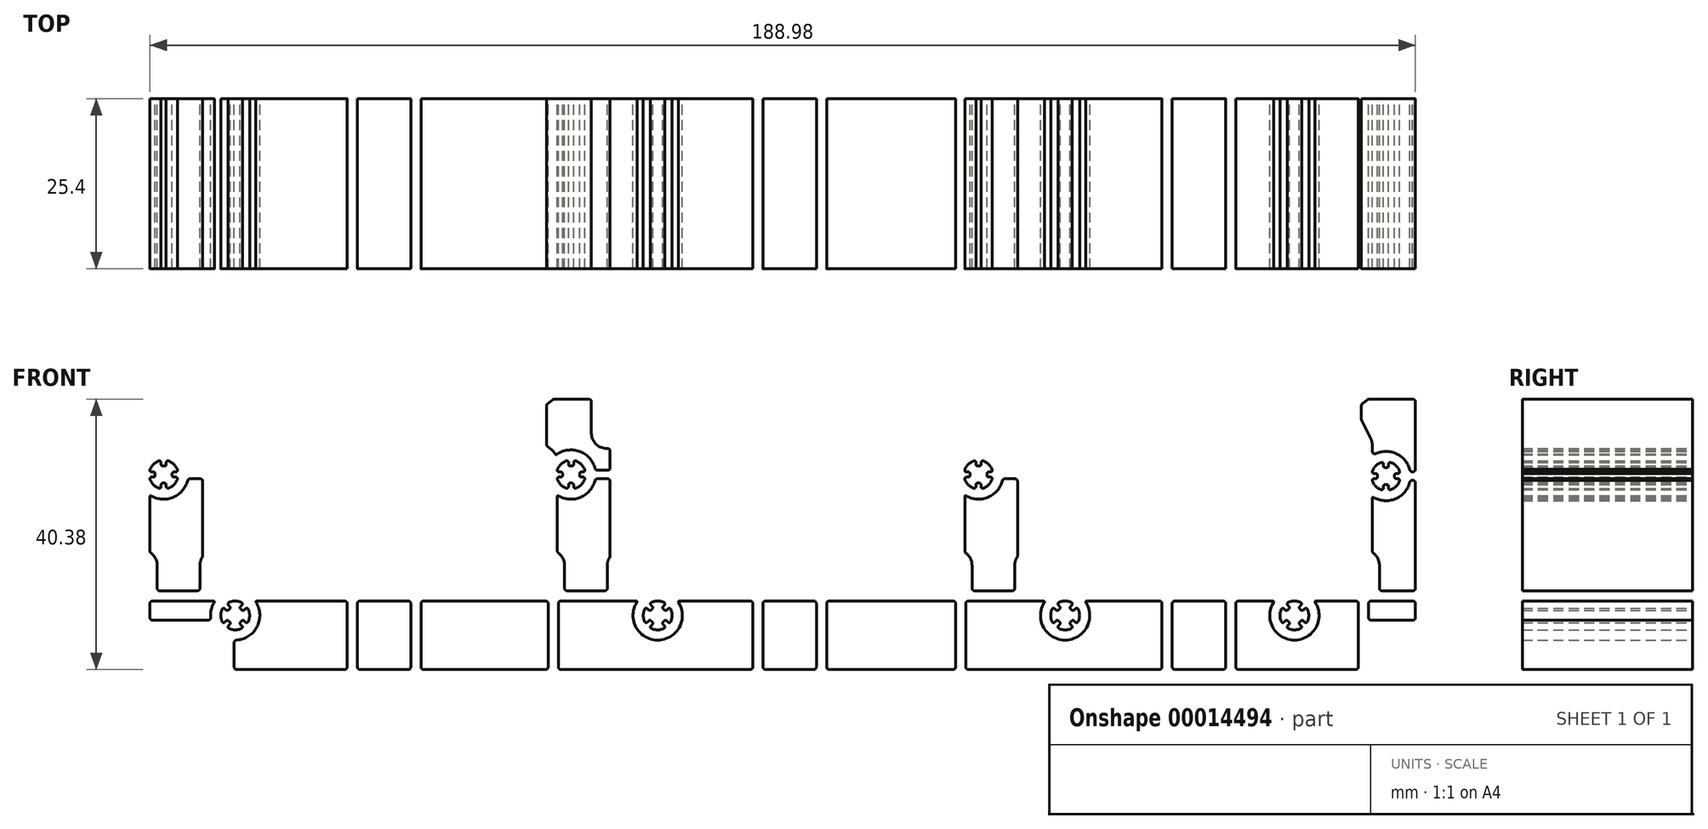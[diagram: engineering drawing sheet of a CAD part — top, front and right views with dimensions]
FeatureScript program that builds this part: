
annotation { "Feature Type Name" : "Feature", "Feature Type Description" : "" }
export const myFeature = defineFeature(function(context is Context, id is Id, definition is map)
    precondition{}
    {
        {
            var Q0;
            Q0=qCreatedBy(makeId("Front.planeOp"),FACE);
            var sketch = newSketch(context, id + "F0", { "sketchPlane" : qUnion([Q0])});
            skArc(sketch, "E0", {"start": v(5.84, 2.36) * mm, "mid": v(5.73, 2.63) * mm, "end": v(5.46, 2.75) * mm});
            skLineSegment(sketch, "E1", {"start": v(5.46, 2.75) * mm, "end": v(-1.75, 2.75) * mm});
            skArc(sketch, "E2", {"start": v(-1.75, 2.75) * mm, "mid": v(-2.02, 2.63) * mm, "end": v(-2.13, 2.36) * mm});
            skLineSegment(sketch, "E3", {"start": v(-2.13, 2.36) * mm, "end": v(-2.13, -7.1) * mm});
            skArc(sketch, "E4", {"start": v(-2.13, -7.1) * mm, "mid": v(-2.02, -7.38) * mm, "end": v(-1.75, -7.5) * mm});
            skLineSegment(sketch, "E5", {"start": v(-1.75, -7.5) * mm, "end": v(5.46, -7.5) * mm});
            skArc(sketch, "E6", {"start": v(5.46, -7.5) * mm, "mid": v(5.73, -7.38) * mm, "end": v(5.84, -7.1) * mm});
            skLineSegment(sketch, "E7", {"start": v(5.84, -7.1) * mm, "end": v(5.84, 2.36) * mm});
            skArc(sketch, "E8", {"start": v(-3.66, 2.36) * mm, "mid": v(-3.77, 2.63) * mm, "end": v(-4.04, 2.75) * mm});
            skLineSegment(sketch, "E9", {"start": v(-4.04, 2.75) * mm, "end": v(-14.63, 2.75) * mm});
            skArc(sketch, "E10", {"start": v(-14.63, 2.75) * mm, "mid": v(-14.74, 2.68) * mm, "end": v(-14.74, 2.55) * mm});
            skArc(sketch, "E11", {"start": v(-20.97, 2.55) * mm, "mid": v(-17.85, -3.1) * mm, "end": v(-14.74, 2.55) * mm});
            skArc(sketch, "E12", {"start": v(-20.97, 2.55) * mm, "mid": v(-20.96, 2.68) * mm, "end": v(-21.07, 2.75) * mm});
            skLineSegment(sketch, "E13", {"start": v(-21.07, 2.75) * mm, "end": v(-32.3, 2.75) * mm});
            skArc(sketch, "E14", {"start": v(-32.3, 2.75) * mm, "mid": v(-32.58, 2.63) * mm, "end": v(-32.69, 2.36) * mm});
            skLineSegment(sketch, "E15", {"start": v(-32.69, 2.36) * mm, "end": v(-32.69, -7.1) * mm});
            skArc(sketch, "E16", {"start": v(-32.69, -7.1) * mm, "mid": v(-32.58, -7.38) * mm, "end": v(-32.3, -7.5) * mm});
            skLineSegment(sketch, "E17", {"start": v(-32.3, -7.5) * mm, "end": v(-4.04, -7.5) * mm});
            skArc(sketch, "E18", {"start": v(-4.04, -7.5) * mm, "mid": v(-3.77, -7.38) * mm, "end": v(-3.66, -7.1) * mm});
            skLineSegment(sketch, "E19", {"start": v(-3.66, -7.1) * mm, "end": v(-3.66, 2.36) * mm});
            skArc(sketch, "E20", {"start": v(-15.9, 1.51) * mm, "mid": v(-16.1, 1.66) * mm, "end": v(-16.31, 1.58) * mm});
            skLineSegment(sketch, "E21", {"start": v(-16.31, 1.58) * mm, "end": v(-16.5, 1.4) * mm});
            skArc(sketch, "E22", {"start": v(-16.87, 1.4) * mm, "mid": v(-16.69, 1.32) * mm, "end": v(-16.5, 1.4) * mm});
            skLineSegment(sketch, "E23", {"start": v(-16.87, 1.4) * mm, "end": v(-17.04, 1.57) * mm});
            skArc(sketch, "E24", {"start": v(-17.04, 1.93) * mm, "mid": v(-17.12, 1.75) * mm, "end": v(-17.04, 1.57) * mm});
            skLineSegment(sketch, "E25", {"start": v(-17.04, 1.93) * mm, "end": v(-16.85, 2.12) * mm});
            skArc(sketch, "E26", {"start": v(-16.85, 2.12) * mm, "mid": v(-16.78, 2.35) * mm, "end": v(-16.92, 2.53) * mm});
            skArc(sketch, "E27", {"start": v(-16.92, 2.53) * mm, "mid": v(-17.85, 2.74) * mm, "end": v(-18.78, 2.53) * mm});
            skArc(sketch, "E28", {"start": v(-18.78, 2.53) * mm, "mid": v(-18.92, 2.35) * mm, "end": v(-18.85, 2.12) * mm});
            skLineSegment(sketch, "E29", {"start": v(-18.85, 2.12) * mm, "end": v(-18.66, 1.93) * mm});
            skArc(sketch, "E30", {"start": v(-18.66, 1.57) * mm, "mid": v(-18.59, 1.75) * mm, "end": v(-18.66, 1.93) * mm});
            skLineSegment(sketch, "E31", {"start": v(-18.66, 1.57) * mm, "end": v(-18.84, 1.4) * mm});
            skArc(sketch, "E32", {"start": v(-19.2, 1.4) * mm, "mid": v(-19.02, 1.32) * mm, "end": v(-18.84, 1.4) * mm});
            skLineSegment(sketch, "E33", {"start": v(-19.2, 1.4) * mm, "end": v(-19.4, 1.58) * mm});
            skArc(sketch, "E34", {"start": v(-19.4, 1.58) * mm, "mid": v(-19.62, 1.66) * mm, "end": v(-19.8, 1.51) * mm});
            skArc(sketch, "E35", {"start": v(-19.8, 1.51) * mm, "mid": v(-20.01, 0.58) * mm, "end": v(-19.8, -0.35) * mm});
            skArc(sketch, "E36", {"start": v(-19.8, -0.35) * mm, "mid": v(-19.62, -0.49) * mm, "end": v(-19.4, -0.42) * mm});
            skLineSegment(sketch, "E37", {"start": v(-19.4, -0.42) * mm, "end": v(-19.2, -0.22) * mm});
            skArc(sketch, "E38", {"start": v(-18.84, -0.22) * mm, "mid": v(-19.02, -0.15) * mm, "end": v(-19.2, -0.22) * mm});
            skLineSegment(sketch, "E39", {"start": v(-18.84, -0.22) * mm, "end": v(-18.66, -0.4) * mm});
            skArc(sketch, "E40", {"start": v(-18.66, -0.76) * mm, "mid": v(-18.59, -0.58) * mm, "end": v(-18.66, -0.4) * mm});
            skLineSegment(sketch, "E41", {"start": v(-18.66, -0.76) * mm, "end": v(-18.85, -0.96) * mm});
            skArc(sketch, "E42", {"start": v(-18.85, -0.96) * mm, "mid": v(-18.92, -1.18) * mm, "end": v(-18.78, -1.36) * mm});
            skArc(sketch, "E43", {"start": v(-18.78, -1.36) * mm, "mid": v(-17.85, -1.57) * mm, "end": v(-16.92, -1.36) * mm});
            skArc(sketch, "E44", {"start": v(-16.92, -1.36) * mm, "mid": v(-16.78, -1.18) * mm, "end": v(-16.85, -0.96) * mm});
            skLineSegment(sketch, "E45", {"start": v(-16.85, -0.96) * mm, "end": v(-17.04, -0.76) * mm});
            skArc(sketch, "E46", {"start": v(-17.04, -0.4) * mm, "mid": v(-17.12, -0.58) * mm, "end": v(-17.04, -0.76) * mm});
            skLineSegment(sketch, "E47", {"start": v(-17.04, -0.4) * mm, "end": v(-16.87, -0.22) * mm});
            skArc(sketch, "E48", {"start": v(-16.5, -0.22) * mm, "mid": v(-16.69, -0.15) * mm, "end": v(-16.87, -0.22) * mm});
            skLineSegment(sketch, "E49", {"start": v(-16.5, -0.22) * mm, "end": v(-16.31, -0.42) * mm});
            skArc(sketch, "E50", {"start": v(-16.31, -0.42) * mm, "mid": v(-16.1, -0.49) * mm, "end": v(-15.9, -0.35) * mm});
            skArc(sketch, "E51", {"start": v(-15.9, -0.35) * mm, "mid": v(-15.7, 0.58) * mm, "end": v(-15.9, 1.51) * mm});
            skArc(sketch, "E52", {"start": v(-34.21, 2.36) * mm, "mid": v(-34.32, 2.63) * mm, "end": v(-34.6, 2.75) * mm});
            skLineSegment(sketch, "E53", {"start": v(-34.6, 2.75) * mm, "end": v(-52.82, 2.75) * mm});
            skArc(sketch, "E54", {"start": v(-52.82, 2.75) * mm, "mid": v(-53.09, 2.63) * mm, "end": v(-53.2, 2.36) * mm});
            skLineSegment(sketch, "E55", {"start": v(-53.2, 2.36) * mm, "end": v(-53.2, -7.1) * mm});
            skArc(sketch, "E56", {"start": v(-53.2, -7.1) * mm, "mid": v(-53.09, -7.38) * mm, "end": v(-52.82, -7.5) * mm});
            skLineSegment(sketch, "E57", {"start": v(-52.82, -7.5) * mm, "end": v(-34.6, -7.5) * mm});
            skArc(sketch, "E58", {"start": v(-34.6, -7.5) * mm, "mid": v(-34.32, -7.38) * mm, "end": v(-34.21, -7.1) * mm});
            skLineSegment(sketch, "E59", {"start": v(-34.21, -7.1) * mm, "end": v(-34.21, 2.36) * mm});
            skArc(sketch, "E60", {"start": v(-54.72, 2.36) * mm, "mid": v(-54.84, 2.63) * mm, "end": v(-55.1, 2.75) * mm});
            skLineSegment(sketch, "E61", {"start": v(-55.1, 2.75) * mm, "end": v(-62.32, 2.75) * mm});
            skArc(sketch, "E62", {"start": v(-62.32, 2.75) * mm, "mid": v(-62.59, 2.63) * mm, "end": v(-62.7, 2.36) * mm});
            skLineSegment(sketch, "E63", {"start": v(-62.7, 2.36) * mm, "end": v(-62.7, -7.1) * mm});
            skArc(sketch, "E64", {"start": v(-62.7, -7.1) * mm, "mid": v(-62.59, -7.38) * mm, "end": v(-62.32, -7.5) * mm});
            skLineSegment(sketch, "E65", {"start": v(-62.32, -7.5) * mm, "end": v(-55.1, -7.5) * mm});
            skArc(sketch, "E66", {"start": v(-55.1, -7.5) * mm, "mid": v(-54.84, -7.38) * mm, "end": v(-54.72, -7.1) * mm});
            skLineSegment(sketch, "E67", {"start": v(-54.72, -7.1) * mm, "end": v(-54.72, 2.36) * mm});
            skArc(sketch, "E68", {"start": v(-64.22, 2.36) * mm, "mid": v(-64.33, 2.63) * mm, "end": v(-64.6, 2.75) * mm});
            skLineSegment(sketch, "E69", {"start": v(-64.6, 2.75) * mm, "end": v(-77.73, 2.75) * mm});
            skArc(sketch, "E70", {"start": v(-77.73, 2.75) * mm, "mid": v(-77.84, 2.68) * mm, "end": v(-77.84, 2.55) * mm});
            skArc(sketch, "E71", {"start": v(-80.74, -3.1) * mm, "mid": v(-77.68, -1.1) * mm, "end": v(-77.84, 2.55) * mm});
            skArc(sketch, "E72", {"start": v(-80.74, -3.1) * mm, "mid": v(-81, -3.2) * mm, "end": v(-81.1, -3.47) * mm});
            skLineSegment(sketch, "E73", {"start": v(-81.1, -3.47) * mm, "end": v(-81.1, -7.1) * mm});
            skArc(sketch, "E74", {"start": v(-81.1, -7.1) * mm, "mid": v(-81, -7.38) * mm, "end": v(-80.72, -7.5) * mm});
            skLineSegment(sketch, "E75", {"start": v(-80.72, -7.5) * mm, "end": v(-64.6, -7.5) * mm});
            skArc(sketch, "E76", {"start": v(-64.6, -7.5) * mm, "mid": v(-64.33, -7.38) * mm, "end": v(-64.22, -7.1) * mm});
            skLineSegment(sketch, "E77", {"start": v(-64.22, -7.1) * mm, "end": v(-64.22, 2.36) * mm});
            skArc(sketch, "E78", {"start": v(-79, 1.52) * mm, "mid": v(-79.19, 1.66) * mm, "end": v(-79.41, 1.59) * mm});
            skLineSegment(sketch, "E79", {"start": v(-79.41, 1.59) * mm, "end": v(-79.6, 1.4) * mm});
            skArc(sketch, "E80", {"start": v(-79.96, 1.4) * mm, "mid": v(-79.78, 1.32) * mm, "end": v(-79.6, 1.4) * mm});
            skLineSegment(sketch, "E81", {"start": v(-79.96, 1.4) * mm, "end": v(-80.14, 1.57) * mm});
            skArc(sketch, "E82", {"start": v(-80.14, 1.93) * mm, "mid": v(-80.22, 1.75) * mm, "end": v(-80.14, 1.57) * mm});
            skLineSegment(sketch, "E83", {"start": v(-80.14, 1.93) * mm, "end": v(-79.95, 2.13) * mm});
            skArc(sketch, "E84", {"start": v(-79.95, 2.13) * mm, "mid": v(-79.88, 2.35) * mm, "end": v(-80.02, 2.53) * mm});
            skArc(sketch, "E85", {"start": v(-80.02, 2.53) * mm, "mid": v(-80.95, 2.75) * mm, "end": v(-81.88, 2.53) * mm});
            skArc(sketch, "E86", {"start": v(-81.88, 2.53) * mm, "mid": v(-82.02, 2.35) * mm, "end": v(-81.95, 2.13) * mm});
            skLineSegment(sketch, "E87", {"start": v(-81.95, 2.13) * mm, "end": v(-81.76, 1.93) * mm});
            skArc(sketch, "E88", {"start": v(-81.76, 1.57) * mm, "mid": v(-81.69, 1.75) * mm, "end": v(-81.76, 1.93) * mm});
            skLineSegment(sketch, "E89", {"start": v(-81.76, 1.57) * mm, "end": v(-81.94, 1.4) * mm});
            skArc(sketch, "E90", {"start": v(-82.3, 1.4) * mm, "mid": v(-82.12, 1.32) * mm, "end": v(-81.94, 1.4) * mm});
            skLineSegment(sketch, "E91", {"start": v(-82.3, 1.4) * mm, "end": v(-82.5, 1.59) * mm});
            skArc(sketch, "E92", {"start": v(-82.5, 1.59) * mm, "mid": v(-82.71, 1.66) * mm, "end": v(-82.9, 1.52) * mm});
            skArc(sketch, "E93", {"start": v(-82.9, 1.52) * mm, "mid": v(-83.11, 0.59) * mm, "end": v(-82.9, -0.34) * mm});
            skArc(sketch, "E94", {"start": v(-82.9, -0.34) * mm, "mid": v(-82.71, -0.49) * mm, "end": v(-82.5, -0.41) * mm});
            skLineSegment(sketch, "E95", {"start": v(-82.5, -0.41) * mm, "end": v(-82.3, -0.22) * mm});
            skArc(sketch, "E96", {"start": v(-81.94, -0.22) * mm, "mid": v(-82.12, -0.15) * mm, "end": v(-82.3, -0.22) * mm});
            skLineSegment(sketch, "E97", {"start": v(-81.94, -0.22) * mm, "end": v(-81.76, -0.4) * mm});
            skArc(sketch, "E98", {"start": v(-81.76, -0.76) * mm, "mid": v(-81.69, -0.58) * mm, "end": v(-81.76, -0.4) * mm});
            skLineSegment(sketch, "E99", {"start": v(-81.76, -0.76) * mm, "end": v(-81.95, -0.95) * mm});
            skArc(sketch, "E100", {"start": v(-81.95, -0.95) * mm, "mid": v(-82.02, -1.18) * mm, "end": v(-81.88, -1.36) * mm});
            skArc(sketch, "E101", {"start": v(-81.88, -1.36) * mm, "mid": v(-80.95, -1.57) * mm, "end": v(-80.02, -1.36) * mm});
            skArc(sketch, "E102", {"start": v(-80.02, -1.36) * mm, "mid": v(-79.88, -1.18) * mm, "end": v(-79.95, -0.95) * mm});
            skLineSegment(sketch, "E103", {"start": v(-79.95, -0.95) * mm, "end": v(-80.14, -0.76) * mm});
            skArc(sketch, "E104", {"start": v(-80.14, -0.4) * mm, "mid": v(-80.22, -0.58) * mm, "end": v(-80.14, -0.76) * mm});
            skLineSegment(sketch, "E105", {"start": v(-80.14, -0.4) * mm, "end": v(-79.96, -0.22) * mm});
            skArc(sketch, "E106", {"start": v(-79.6, -0.22) * mm, "mid": v(-79.78, -0.15) * mm, "end": v(-79.96, -0.22) * mm});
            skLineSegment(sketch, "E107", {"start": v(-79.6, -0.22) * mm, "end": v(-79.41, -0.41) * mm});
            skArc(sketch, "E108", {"start": v(-79.41, -0.41) * mm, "mid": v(-79.19, -0.49) * mm, "end": v(-79, -0.34) * mm});
            skArc(sketch, "E109", {"start": v(-79, -0.34) * mm, "mid": v(-78.8, 0.59) * mm, "end": v(-79, 1.52) * mm});
            skArc(sketch, "E110", {"start": v(-84.07, 2.55) * mm, "mid": v(-84.06, 2.68) * mm, "end": v(-84.17, 2.75) * mm});
            skLineSegment(sketch, "E111", {"start": v(-84.17, 2.75) * mm, "end": v(-93.3, 2.75) * mm});
            skArc(sketch, "E112", {"start": v(-93.3, 2.75) * mm, "mid": v(-93.57, 2.63) * mm, "end": v(-93.68, 2.36) * mm});
            skLineSegment(sketch, "E113", {"start": v(-93.68, 2.36) * mm, "end": v(-93.68, 0.25) * mm});
            skArc(sketch, "E114", {"start": v(-93.68, 0.25) * mm, "mid": v(-93.57, -0.02) * mm, "end": v(-93.3, -0.13) * mm});
            skLineSegment(sketch, "E115", {"start": v(-93.3, -0.13) * mm, "end": v(-85, -0.13) * mm});
            skArc(sketch, "E116", {"start": v(-85, -0.13) * mm, "mid": v(-84.72, 0) * mm, "end": v(-84.62, 0.28) * mm});
            skArc(sketch, "E117", {"start": v(-84.07, 2.55) * mm, "mid": v(-84.53, 1.46) * mm, "end": v(-84.62, 0.28) * mm});
            skArc(sketch, "E118", {"start": v(-85.8, 20.62) * mm, "mid": v(-85.91, 20.89) * mm, "end": v(-86.18, 21) * mm});
            skLineSegment(sketch, "E119", {"start": v(-86.18, 21) * mm, "end": v(-87.7, 21) * mm});
            skArc(sketch, "E120", {"start": v(-87.7, 21) * mm, "mid": v(-87.93, 20.92) * mm, "end": v(-88.07, 20.71) * mm});
            skArc(sketch, "E121", {"start": v(-93.5, 18.46) * mm, "mid": v(-90.22, 18.24) * mm, "end": v(-88.07, 20.71) * mm});
            skArc(sketch, "E122", {"start": v(-93.5, 18.46) * mm, "mid": v(-93.62, 18.46) * mm, "end": v(-93.68, 18.35) * mm});
            skLineSegment(sketch, "E123", {"start": v(-93.68, 18.35) * mm, "end": v(-93.68, 10.22) * mm});
            skArc(sketch, "E124", {"start": v(-93.68, 10.22) * mm, "mid": v(-93.64, 10.05) * mm, "end": v(-93.53, 9.92) * mm});
            skArc(sketch, "E125", {"start": v(-92.6, 8.08) * mm, "mid": v(-92.85, 9.1) * mm, "end": v(-93.53, 9.92) * mm});
            skLineSegment(sketch, "E126", {"start": v(-92.6, 8.08) * mm, "end": v(-92.6, 4.65) * mm});
            skArc(sketch, "E127", {"start": v(-92.6, 4.65) * mm, "mid": v(-92.5, 4.38) * mm, "end": v(-92.22, 4.27) * mm});
            skLineSegment(sketch, "E128", {"start": v(-92.22, 4.27) * mm, "end": v(-86.6, 4.27) * mm});
            skArc(sketch, "E129", {"start": v(-86.6, 4.27) * mm, "mid": v(-86.33, 4.38) * mm, "end": v(-86.22, 4.65) * mm});
            skLineSegment(sketch, "E130", {"start": v(-86.22, 4.65) * mm, "end": v(-86.22, 8.08) * mm});
            skArc(sketch, "E131", {"start": v(-85.86, 9.3) * mm, "mid": v(-86.13, 8.72) * mm, "end": v(-86.22, 8.08) * mm});
            skArc(sketch, "E132", {"start": v(-85.86, 9.3) * mm, "mid": v(-85.82, 9.4) * mm, "end": v(-85.8, 9.51) * mm});
            skLineSegment(sketch, "E133", {"start": v(-85.8, 9.51) * mm, "end": v(-85.8, 20.62) * mm});
            skArc(sketch, "E134", {"start": v(-88.6, 32.5) * mm, "mid": v(-88.7, 32.78) * mm, "end": v(-88.98, 32.9) * mm});
            skLineSegment(sketch, "E135", {"start": v(-88.98, 32.9) * mm, "end": v(-94.18, 32.9) * mm});
            skArc(sketch, "E136", {"start": v(-94.18, 32.9) * mm, "mid": v(-94.3, 32.87) * mm, "end": v(-94.42, 32.8) * mm});
            skLineSegment(sketch, "E137", {"start": v(-94.42, 32.8) * mm, "end": v(-95.16, 32.18) * mm});
            skArc(sketch, "E138", {"start": v(-95.16, 32.18) * mm, "mid": v(-95.26, 32.05) * mm, "end": v(-95.3, 31.89) * mm});
            skLineSegment(sketch, "E139", {"start": v(-95.3, 31.89) * mm, "end": v(-95.3, 26.15) * mm});
            skArc(sketch, "E140", {"start": v(-95.3, 26.15) * mm, "mid": v(-95.26, 25.99) * mm, "end": v(-95.16, 25.86) * mm});
            skLineSegment(sketch, "E141", {"start": v(-95.16, 25.86) * mm, "end": v(-94.5, 25.3) * mm});
            skArc(sketch, "E142", {"start": v(-93.97, 24.66) * mm, "mid": v(-94.2, 25) * mm, "end": v(-94.5, 25.3) * mm});
            skArc(sketch, "E143", {"start": v(-93.97, 24.66) * mm, "mid": v(-93.89, 24.6) * mm, "end": v(-93.79, 24.62) * mm});
            skArc(sketch, "E144", {"start": v(-88.07, 22.56) * mm, "mid": v(-90.38, 25.1) * mm, "end": v(-93.79, 24.62) * mm});
            skArc(sketch, "E145", {"start": v(-88.07, 22.56) * mm, "mid": v(-87.93, 22.35) * mm, "end": v(-87.7, 22.27) * mm});
            skLineSegment(sketch, "E146", {"start": v(-87.7, 22.27) * mm, "end": v(-86.18, 22.27) * mm});
            skArc(sketch, "E147", {"start": v(-86.18, 22.27) * mm, "mid": v(-85.91, 22.38) * mm, "end": v(-85.8, 22.65) * mm});
            skLineSegment(sketch, "E148", {"start": v(-85.8, 22.65) * mm, "end": v(-85.8, 25.14) * mm});
            skArc(sketch, "E149", {"start": v(-85.8, 25.14) * mm, "mid": v(-85.92, 25.42) * mm, "end": v(-86.2, 25.53) * mm});
            skArc(sketch, "E150", {"start": v(-88.6, 27.81) * mm, "mid": v(-87.89, 26.16) * mm, "end": v(-86.2, 25.53) * mm});
            skLineSegment(sketch, "E151", {"start": v(-88.6, 27.81) * mm, "end": v(-88.6, 32.5) * mm});
            skArc(sketch, "E152", {"start": v(-90.1, 22.02) * mm, "mid": v(-90.29, 21.94) * mm, "end": v(-90.36, 21.76) * mm});
            skLineSegment(sketch, "E153", {"start": v(-90.1, 22.02) * mm, "end": v(-89.84, 22.02) * mm});
            skArc(sketch, "E154", {"start": v(-89.84, 22.02) * mm, "mid": v(-89.63, 22.12) * mm, "end": v(-89.6, 22.35) * mm});
            skArc(sketch, "E155", {"start": v(-89.6, 22.35) * mm, "mid": v(-90.1, 23.16) * mm, "end": v(-90.91, 23.67) * mm});
            skArc(sketch, "E156", {"start": v(-90.91, 23.67) * mm, "mid": v(-91.14, 23.64) * mm, "end": v(-91.25, 23.43) * mm});
            skLineSegment(sketch, "E157", {"start": v(-91.25, 23.43) * mm, "end": v(-91.25, 23.16) * mm});
            skArc(sketch, "E158", {"start": v(-91.5, 22.9) * mm, "mid": v(-91.33, 22.98) * mm, "end": v(-91.25, 23.16) * mm});
            skLineSegment(sketch, "E159", {"start": v(-91.5, 22.9) * mm, "end": v(-91.76, 22.9) * mm});
            skArc(sketch, "E160", {"start": v(-92.01, 23.16) * mm, "mid": v(-91.94, 22.98) * mm, "end": v(-91.76, 22.9) * mm});
            skLineSegment(sketch, "E161", {"start": v(-92.01, 23.16) * mm, "end": v(-92.01, 23.43) * mm});
            skArc(sketch, "E162", {"start": v(-92.01, 23.43) * mm, "mid": v(-92.12, 23.64) * mm, "end": v(-92.35, 23.67) * mm});
            skArc(sketch, "E163", {"start": v(-92.35, 23.67) * mm, "mid": v(-93.16, 23.16) * mm, "end": v(-93.67, 22.35) * mm});
            skArc(sketch, "E164", {"start": v(-93.67, 22.35) * mm, "mid": v(-93.64, 22.12) * mm, "end": v(-93.43, 22.02) * mm});
            skLineSegment(sketch, "E165", {"start": v(-93.43, 22.02) * mm, "end": v(-93.16, 22.02) * mm});
            skArc(sketch, "E166", {"start": v(-92.9, 21.76) * mm, "mid": v(-92.98, 21.94) * mm, "end": v(-93.16, 22.02) * mm});
            skLineSegment(sketch, "E167", {"start": v(-92.9, 21.76) * mm, "end": v(-92.9, 21.5) * mm});
            skArc(sketch, "E168", {"start": v(-93.16, 21.25) * mm, "mid": v(-92.98, 21.33) * mm, "end": v(-92.9, 21.5) * mm});
            skLineSegment(sketch, "E169", {"start": v(-93.16, 21.25) * mm, "end": v(-93.43, 21.25) * mm});
            skArc(sketch, "E170", {"start": v(-93.43, 21.25) * mm, "mid": v(-93.64, 21.15) * mm, "end": v(-93.67, 20.92) * mm});
            skArc(sketch, "E171", {"start": v(-93.67, 20.92) * mm, "mid": v(-93.16, 20.1) * mm, "end": v(-92.35, 19.6) * mm});
            skArc(sketch, "E172", {"start": v(-92.35, 19.6) * mm, "mid": v(-92.12, 19.63) * mm, "end": v(-92.01, 19.84) * mm});
            skLineSegment(sketch, "E173", {"start": v(-92.01, 19.84) * mm, "end": v(-92.01, 20.11) * mm});
            skArc(sketch, "E174", {"start": v(-91.76, 20.37) * mm, "mid": v(-91.94, 20.3) * mm, "end": v(-92.01, 20.11) * mm});
            skLineSegment(sketch, "E175", {"start": v(-91.76, 20.37) * mm, "end": v(-91.5, 20.37) * mm});
            skArc(sketch, "E176", {"start": v(-91.25, 20.11) * mm, "mid": v(-91.33, 20.3) * mm, "end": v(-91.5, 20.37) * mm});
            skLineSegment(sketch, "E177", {"start": v(-91.25, 20.11) * mm, "end": v(-91.25, 19.84) * mm});
            skArc(sketch, "E178", {"start": v(-91.25, 19.84) * mm, "mid": v(-91.14, 19.63) * mm, "end": v(-90.91, 19.6) * mm});
            skArc(sketch, "E179", {"start": v(-90.91, 19.6) * mm, "mid": v(-90.1, 20.1) * mm, "end": v(-89.6, 20.92) * mm});
            skArc(sketch, "E180", {"start": v(-89.6, 20.92) * mm, "mid": v(-89.63, 21.15) * mm, "end": v(-89.84, 21.25) * mm});
            skLineSegment(sketch, "E181", {"start": v(-89.84, 21.25) * mm, "end": v(-90.1, 21.25) * mm});
            skArc(sketch, "E182", {"start": v(-90.36, 21.5) * mm, "mid": v(-90.29, 21.33) * mm, "end": v(-90.1, 21.25) * mm});
            skLineSegment(sketch, "E183", {"start": v(-90.36, 21.5) * mm, "end": v(-90.36, 21.76) * mm});
            skArc(sketch, "E184", {"start": v(35.89, 20.62) * mm, "mid": v(35.77, 20.89) * mm, "end": v(35.5, 21) * mm});
            skLineSegment(sketch, "E185", {"start": v(35.5, 21) * mm, "end": v(33.99, 21) * mm});
            skArc(sketch, "E186", {"start": v(33.99, 21) * mm, "mid": v(33.76, 20.92) * mm, "end": v(33.62, 20.71) * mm});
            skArc(sketch, "E187", {"start": v(28.2, 18.46) * mm, "mid": v(31.47, 18.24) * mm, "end": v(33.62, 20.71) * mm});
            skArc(sketch, "E188", {"start": v(28.2, 18.46) * mm, "mid": v(28.07, 18.46) * mm, "end": v(28, 18.35) * mm});
            skLineSegment(sketch, "E189", {"start": v(28, 18.35) * mm, "end": v(28, 10.22) * mm});
            skArc(sketch, "E190", {"start": v(28, 10.22) * mm, "mid": v(28.04, 10.05) * mm, "end": v(28.16, 9.92) * mm});
            skArc(sketch, "E191", {"start": v(29.08, 8.08) * mm, "mid": v(28.84, 9.1) * mm, "end": v(28.16, 9.92) * mm});
            skLineSegment(sketch, "E192", {"start": v(29.08, 8.08) * mm, "end": v(29.08, 4.65) * mm});
            skArc(sketch, "E193", {"start": v(29.08, 4.65) * mm, "mid": v(29.2, 4.38) * mm, "end": v(29.46, 4.27) * mm});
            skLineSegment(sketch, "E194", {"start": v(29.46, 4.27) * mm, "end": v(35.09, 4.27) * mm});
            skArc(sketch, "E195", {"start": v(35.09, 4.27) * mm, "mid": v(35.36, 4.38) * mm, "end": v(35.47, 4.65) * mm});
            skLineSegment(sketch, "E196", {"start": v(35.47, 4.65) * mm, "end": v(35.47, 8.08) * mm});
            skArc(sketch, "E197", {"start": v(35.83, 9.3) * mm, "mid": v(35.56, 8.72) * mm, "end": v(35.47, 8.08) * mm});
            skArc(sketch, "E198", {"start": v(35.83, 9.3) * mm, "mid": v(35.87, 9.4) * mm, "end": v(35.89, 9.51) * mm});
            skLineSegment(sketch, "E199", {"start": v(35.89, 9.51) * mm, "end": v(35.89, 20.62) * mm});
            skArc(sketch, "E200", {"start": v(33.1, 32.5) * mm, "mid": v(32.98, 32.78) * mm, "end": v(32.71, 32.9) * mm});
            skLineSegment(sketch, "E201", {"start": v(32.71, 32.9) * mm, "end": v(27.5, 32.9) * mm});
            skArc(sketch, "E202", {"start": v(27.5, 32.9) * mm, "mid": v(27.38, 32.87) * mm, "end": v(27.26, 32.8) * mm});
            skLineSegment(sketch, "E203", {"start": v(27.26, 32.8) * mm, "end": v(26.52, 32.18) * mm});
            skArc(sketch, "E204", {"start": v(26.52, 32.18) * mm, "mid": v(26.42, 32.05) * mm, "end": v(26.39, 31.89) * mm});
            skLineSegment(sketch, "E205", {"start": v(26.39, 31.89) * mm, "end": v(26.39, 26.15) * mm});
            skArc(sketch, "E206", {"start": v(26.39, 26.15) * mm, "mid": v(26.42, 25.99) * mm, "end": v(26.52, 25.86) * mm});
            skLineSegment(sketch, "E207", {"start": v(26.52, 25.86) * mm, "end": v(27.19, 25.3) * mm});
            skArc(sketch, "E208", {"start": v(27.71, 24.66) * mm, "mid": v(27.48, 25) * mm, "end": v(27.19, 25.3) * mm});
            skArc(sketch, "E209", {"start": v(27.71, 24.66) * mm, "mid": v(27.8, 24.6) * mm, "end": v(27.9, 24.62) * mm});
            skArc(sketch, "E210", {"start": v(33.62, 22.56) * mm, "mid": v(31.3, 25.1) * mm, "end": v(27.9, 24.62) * mm});
            skArc(sketch, "E211", {"start": v(33.62, 22.56) * mm, "mid": v(33.76, 22.35) * mm, "end": v(33.99, 22.27) * mm});
            skLineSegment(sketch, "E212", {"start": v(33.99, 22.27) * mm, "end": v(35.5, 22.27) * mm});
            skArc(sketch, "E213", {"start": v(35.5, 22.27) * mm, "mid": v(35.77, 22.38) * mm, "end": v(35.89, 22.65) * mm});
            skLineSegment(sketch, "E214", {"start": v(35.89, 22.65) * mm, "end": v(35.89, 25.14) * mm});
            skArc(sketch, "E215", {"start": v(35.89, 25.14) * mm, "mid": v(35.77, 25.42) * mm, "end": v(35.49, 25.53) * mm});
            skArc(sketch, "E216", {"start": v(33.1, 27.81) * mm, "mid": v(33.8, 26.16) * mm, "end": v(35.49, 25.53) * mm});
            skLineSegment(sketch, "E217", {"start": v(33.1, 27.81) * mm, "end": v(33.1, 32.5) * mm});
            skLineSegment(sketch, "E218", {"start": v(31.32, 21.5) * mm, "end": v(31.32, 21.76) * mm});
            skArc(sketch, "E219", {"start": v(31.58, 22.02) * mm, "mid": v(31.4, 21.94) * mm, "end": v(31.32, 21.76) * mm});
            skLineSegment(sketch, "E220", {"start": v(31.58, 22.02) * mm, "end": v(31.85, 22.02) * mm});
            skArc(sketch, "E221", {"start": v(31.85, 22.02) * mm, "mid": v(32.06, 22.12) * mm, "end": v(32.09, 22.35) * mm});
            skArc(sketch, "E222", {"start": v(32.09, 22.35) * mm, "mid": v(31.58, 23.16) * mm, "end": v(30.77, 23.67) * mm});
            skArc(sketch, "E223", {"start": v(30.77, 23.67) * mm, "mid": v(30.54, 23.64) * mm, "end": v(30.43, 23.43) * mm});
            skLineSegment(sketch, "E224", {"start": v(30.43, 23.43) * mm, "end": v(30.43, 23.16) * mm});
            skArc(sketch, "E225", {"start": v(30.18, 22.9) * mm, "mid": v(30.36, 22.98) * mm, "end": v(30.43, 23.16) * mm});
            skLineSegment(sketch, "E226", {"start": v(30.18, 22.9) * mm, "end": v(29.93, 22.9) * mm});
            skArc(sketch, "E227", {"start": v(29.67, 23.16) * mm, "mid": v(29.75, 22.98) * mm, "end": v(29.93, 22.9) * mm});
            skLineSegment(sketch, "E228", {"start": v(29.67, 23.16) * mm, "end": v(29.67, 23.43) * mm});
            skArc(sketch, "E229", {"start": v(29.67, 23.43) * mm, "mid": v(29.57, 23.64) * mm, "end": v(29.33, 23.67) * mm});
            skArc(sketch, "E230", {"start": v(29.33, 23.67) * mm, "mid": v(28.53, 23.16) * mm, "end": v(28.02, 22.35) * mm});
            skArc(sketch, "E231", {"start": v(28.02, 22.35) * mm, "mid": v(28.05, 22.12) * mm, "end": v(28.26, 22.02) * mm});
            skLineSegment(sketch, "E232", {"start": v(28.26, 22.02) * mm, "end": v(28.53, 22.02) * mm});
            skArc(sketch, "E233", {"start": v(28.78, 21.76) * mm, "mid": v(28.7, 21.94) * mm, "end": v(28.53, 22.02) * mm});
            skLineSegment(sketch, "E234", {"start": v(28.78, 21.76) * mm, "end": v(28.78, 21.5) * mm});
            skArc(sketch, "E235", {"start": v(28.53, 21.25) * mm, "mid": v(28.7, 21.33) * mm, "end": v(28.78, 21.5) * mm});
            skLineSegment(sketch, "E236", {"start": v(28.53, 21.25) * mm, "end": v(28.26, 21.25) * mm});
            skArc(sketch, "E237", {"start": v(28.26, 21.25) * mm, "mid": v(28.05, 21.15) * mm, "end": v(28.02, 20.92) * mm});
            skArc(sketch, "E238", {"start": v(28.02, 20.92) * mm, "mid": v(28.53, 20.1) * mm, "end": v(29.33, 19.6) * mm});
            skArc(sketch, "E239", {"start": v(29.33, 19.6) * mm, "mid": v(29.57, 19.63) * mm, "end": v(29.67, 19.84) * mm});
            skLineSegment(sketch, "E240", {"start": v(29.67, 19.84) * mm, "end": v(29.67, 20.11) * mm});
            skArc(sketch, "E241", {"start": v(29.93, 20.37) * mm, "mid": v(29.75, 20.3) * mm, "end": v(29.67, 20.11) * mm});
            skLineSegment(sketch, "E242", {"start": v(29.93, 20.37) * mm, "end": v(30.18, 20.37) * mm});
            skArc(sketch, "E243", {"start": v(30.43, 20.11) * mm, "mid": v(30.36, 20.3) * mm, "end": v(30.18, 20.37) * mm});
            skLineSegment(sketch, "E244", {"start": v(30.43, 20.11) * mm, "end": v(30.43, 19.84) * mm});
            skArc(sketch, "E245", {"start": v(30.43, 19.84) * mm, "mid": v(30.54, 19.63) * mm, "end": v(30.77, 19.6) * mm});
            skArc(sketch, "E246", {"start": v(30.77, 19.6) * mm, "mid": v(31.58, 20.1) * mm, "end": v(32.09, 20.92) * mm});
            skArc(sketch, "E247", {"start": v(32.09, 20.92) * mm, "mid": v(32.06, 21.15) * mm, "end": v(31.85, 21.25) * mm});
            skLineSegment(sketch, "E248", {"start": v(31.85, 21.25) * mm, "end": v(31.58, 21.25) * mm});
            skArc(sketch, "E249", {"start": v(31.32, 21.5) * mm, "mid": v(31.4, 21.33) * mm, "end": v(31.58, 21.25) * mm});
            skArc(sketch, "E250", {"start": v(44.94, 1.52) * mm, "mid": v(44.75, 1.66) * mm, "end": v(44.53, 1.59) * mm});
            skLineSegment(sketch, "E251", {"start": v(44.53, 1.59) * mm, "end": v(44.34, 1.4) * mm});
            skArc(sketch, "E252", {"start": v(43.98, 1.4) * mm, "mid": v(44.16, 1.32) * mm, "end": v(44.34, 1.4) * mm});
            skLineSegment(sketch, "E253", {"start": v(43.98, 1.4) * mm, "end": v(43.8, 1.57) * mm});
            skArc(sketch, "E254", {"start": v(43.8, 1.93) * mm, "mid": v(43.72, 1.75) * mm, "end": v(43.8, 1.57) * mm});
            skLineSegment(sketch, "E255", {"start": v(43.8, 1.93) * mm, "end": v(44, 2.13) * mm});
            skArc(sketch, "E256", {"start": v(44, 2.13) * mm, "mid": v(44.06, 2.35) * mm, "end": v(43.92, 2.53) * mm});
            skArc(sketch, "E257", {"start": v(43.92, 2.53) * mm, "mid": v(42.99, 2.75) * mm, "end": v(42.06, 2.53) * mm});
            skArc(sketch, "E258", {"start": v(42.06, 2.53) * mm, "mid": v(41.92, 2.35) * mm, "end": v(41.99, 2.13) * mm});
            skLineSegment(sketch, "E259", {"start": v(41.99, 2.13) * mm, "end": v(42.18, 1.93) * mm});
            skArc(sketch, "E260", {"start": v(42.18, 1.57) * mm, "mid": v(42.26, 1.75) * mm, "end": v(42.18, 1.93) * mm});
            skLineSegment(sketch, "E261", {"start": v(42.18, 1.57) * mm, "end": v(42, 1.4) * mm});
            skArc(sketch, "E262", {"start": v(41.64, 1.4) * mm, "mid": v(41.82, 1.32) * mm, "end": v(42, 1.4) * mm});
            skLineSegment(sketch, "E263", {"start": v(41.64, 1.4) * mm, "end": v(41.45, 1.59) * mm});
            skArc(sketch, "E264", {"start": v(41.45, 1.59) * mm, "mid": v(41.23, 1.66) * mm, "end": v(41.04, 1.52) * mm});
            skArc(sketch, "E265", {"start": v(41.04, 1.52) * mm, "mid": v(40.83, 0.59) * mm, "end": v(41.04, -0.34) * mm});
            skArc(sketch, "E266", {"start": v(41.04, -0.34) * mm, "mid": v(41.23, -0.49) * mm, "end": v(41.45, -0.41) * mm});
            skLineSegment(sketch, "E267", {"start": v(41.45, -0.41) * mm, "end": v(41.64, -0.22) * mm});
            skArc(sketch, "E268", {"start": v(42, -0.22) * mm, "mid": v(41.82, -0.15) * mm, "end": v(41.64, -0.22) * mm});
            skLineSegment(sketch, "E269", {"start": v(42, -0.22) * mm, "end": v(42.18, -0.4) * mm});
            skArc(sketch, "E270", {"start": v(42.18, -0.76) * mm, "mid": v(42.26, -0.58) * mm, "end": v(42.18, -0.4) * mm});
            skLineSegment(sketch, "E271", {"start": v(42.18, -0.76) * mm, "end": v(41.99, -0.95) * mm});
            skArc(sketch, "E272", {"start": v(41.99, -0.95) * mm, "mid": v(41.92, -1.18) * mm, "end": v(42.06, -1.36) * mm});
            skArc(sketch, "E273", {"start": v(42.06, -1.36) * mm, "mid": v(42.99, -1.57) * mm, "end": v(43.92, -1.36) * mm});
            skArc(sketch, "E274", {"start": v(43.92, -1.36) * mm, "mid": v(44.06, -1.18) * mm, "end": v(44, -0.95) * mm});
            skLineSegment(sketch, "E275", {"start": v(44, -0.95) * mm, "end": v(43.8, -0.76) * mm});
            skArc(sketch, "E276", {"start": v(43.8, -0.4) * mm, "mid": v(43.72, -0.58) * mm, "end": v(43.8, -0.76) * mm});
            skLineSegment(sketch, "E277", {"start": v(43.8, -0.4) * mm, "end": v(43.98, -0.22) * mm});
            skArc(sketch, "E278", {"start": v(44.34, -0.22) * mm, "mid": v(44.16, -0.15) * mm, "end": v(43.98, -0.22) * mm});
            skLineSegment(sketch, "E279", {"start": v(44.34, -0.22) * mm, "end": v(44.53, -0.41) * mm});
            skArc(sketch, "E280", {"start": v(44.53, -0.41) * mm, "mid": v(44.75, -0.49) * mm, "end": v(44.94, -0.34) * mm});
            skArc(sketch, "E281", {"start": v(44.94, -0.34) * mm, "mid": v(45.15, 0.59) * mm, "end": v(44.94, 1.52) * mm});
            skArc(sketch, "E282", {"start": v(66.96, 2.36) * mm, "mid": v(66.85, 2.63) * mm, "end": v(66.58, 2.75) * mm});
            skLineSegment(sketch, "E283", {"start": v(66.58, 2.75) * mm, "end": v(59.37, 2.75) * mm});
            skArc(sketch, "E284", {"start": v(59.37, 2.75) * mm, "mid": v(59.1, 2.63) * mm, "end": v(58.99, 2.36) * mm});
            skLineSegment(sketch, "E285", {"start": v(58.99, 2.36) * mm, "end": v(58.99, -7.1) * mm});
            skArc(sketch, "E286", {"start": v(58.99, -7.1) * mm, "mid": v(59.1, -7.38) * mm, "end": v(59.37, -7.5) * mm});
            skLineSegment(sketch, "E287", {"start": v(59.37, -7.5) * mm, "end": v(66.58, -7.5) * mm});
            skArc(sketch, "E288", {"start": v(66.58, -7.5) * mm, "mid": v(66.85, -7.38) * mm, "end": v(66.96, -7.1) * mm});
            skLineSegment(sketch, "E289", {"start": v(66.96, -7.1) * mm, "end": v(66.96, 2.36) * mm});
            skArc(sketch, "E290", {"start": v(57.46, 2.36) * mm, "mid": v(57.35, 2.63) * mm, "end": v(57.08, 2.75) * mm});
            skLineSegment(sketch, "E291", {"start": v(57.08, 2.75) * mm, "end": v(46.21, 2.75) * mm});
            skArc(sketch, "E292", {"start": v(46.21, 2.75) * mm, "mid": v(46.1, 2.68) * mm, "end": v(46.1, 2.55) * mm});
            skArc(sketch, "E293", {"start": v(39.87, 2.55) * mm, "mid": v(42.99, -3.1) * mm, "end": v(46.1, 2.55) * mm});
            skArc(sketch, "E294", {"start": v(39.87, 2.55) * mm, "mid": v(39.88, 2.68) * mm, "end": v(39.77, 2.75) * mm});
            skLineSegment(sketch, "E295", {"start": v(39.77, 2.75) * mm, "end": v(28.54, 2.75) * mm});
            skArc(sketch, "E296", {"start": v(28.54, 2.75) * mm, "mid": v(28.27, 2.63) * mm, "end": v(28.16, 2.36) * mm});
            skLineSegment(sketch, "E297", {"start": v(28.16, 2.36) * mm, "end": v(28.16, -7.1) * mm});
            skArc(sketch, "E298", {"start": v(28.16, -7.1) * mm, "mid": v(28.27, -7.38) * mm, "end": v(28.54, -7.5) * mm});
            skLineSegment(sketch, "E299", {"start": v(28.54, -7.5) * mm, "end": v(57.08, -7.5) * mm});
            skArc(sketch, "E300", {"start": v(57.08, -7.5) * mm, "mid": v(57.35, -7.38) * mm, "end": v(57.46, -7.1) * mm});
            skLineSegment(sketch, "E301", {"start": v(57.46, -7.1) * mm, "end": v(57.46, 2.36) * mm});
            skArc(sketch, "E302", {"start": v(26.63, 2.36) * mm, "mid": v(26.52, 2.63) * mm, "end": v(26.25, 2.75) * mm});
            skLineSegment(sketch, "E303", {"start": v(26.25, 2.75) * mm, "end": v(7.75, 2.75) * mm});
            skArc(sketch, "E304", {"start": v(7.75, 2.75) * mm, "mid": v(7.48, 2.63) * mm, "end": v(7.37, 2.36) * mm});
            skLineSegment(sketch, "E305", {"start": v(7.37, 2.36) * mm, "end": v(7.37, -7.1) * mm});
            skArc(sketch, "E306", {"start": v(7.37, -7.1) * mm, "mid": v(7.48, -7.38) * mm, "end": v(7.75, -7.5) * mm});
            skLineSegment(sketch, "E307", {"start": v(7.75, -7.5) * mm, "end": v(26.25, -7.5) * mm});
            skArc(sketch, "E308", {"start": v(26.25, -7.5) * mm, "mid": v(26.52, -7.38) * mm, "end": v(26.63, -7.1) * mm});
            skLineSegment(sketch, "E309", {"start": v(26.63, -7.1) * mm, "end": v(26.63, 2.36) * mm});
            skArc(sketch, "E310", {"start": v(86.78, 2.36) * mm, "mid": v(86.67, 2.63) * mm, "end": v(86.4, 2.75) * mm});
            skLineSegment(sketch, "E311", {"start": v(86.4, 2.75) * mm, "end": v(80.45, 2.75) * mm});
            skArc(sketch, "E312", {"start": v(80.45, 2.75) * mm, "mid": v(80.34, 2.68) * mm, "end": v(80.34, 2.55) * mm});
            skArc(sketch, "E313", {"start": v(74.11, 2.55) * mm, "mid": v(77.23, -3.1) * mm, "end": v(80.34, 2.55) * mm});
            skArc(sketch, "E314", {"start": v(74.11, 2.55) * mm, "mid": v(74.12, 2.68) * mm, "end": v(74, 2.75) * mm});
            skLineSegment(sketch, "E315", {"start": v(74, 2.75) * mm, "end": v(68.87, 2.75) * mm});
            skArc(sketch, "E316", {"start": v(68.87, 2.75) * mm, "mid": v(68.6, 2.63) * mm, "end": v(68.49, 2.36) * mm});
            skLineSegment(sketch, "E317", {"start": v(68.49, 2.36) * mm, "end": v(68.49, -7.1) * mm});
            skArc(sketch, "E318", {"start": v(68.49, -7.1) * mm, "mid": v(68.6, -7.38) * mm, "end": v(68.87, -7.5) * mm});
            skLineSegment(sketch, "E319", {"start": v(68.87, -7.5) * mm, "end": v(86.4, -7.5) * mm});
            skArc(sketch, "E320", {"start": v(86.4, -7.5) * mm, "mid": v(86.67, -7.38) * mm, "end": v(86.78, -7.1) * mm});
            skLineSegment(sketch, "E321", {"start": v(86.78, -7.1) * mm, "end": v(86.78, 2.36) * mm});
            skArc(sketch, "E322", {"start": v(79.18, 1.52) * mm, "mid": v(79, 1.66) * mm, "end": v(78.77, 1.59) * mm});
            skLineSegment(sketch, "E323", {"start": v(78.77, 1.59) * mm, "end": v(78.58, 1.4) * mm});
            skArc(sketch, "E324", {"start": v(78.22, 1.4) * mm, "mid": v(78.4, 1.32) * mm, "end": v(78.58, 1.4) * mm});
            skLineSegment(sketch, "E325", {"start": v(78.22, 1.4) * mm, "end": v(78.04, 1.57) * mm});
            skArc(sketch, "E326", {"start": v(78.04, 1.93) * mm, "mid": v(77.96, 1.75) * mm, "end": v(78.04, 1.57) * mm});
            skLineSegment(sketch, "E327", {"start": v(78.04, 1.93) * mm, "end": v(78.23, 2.13) * mm});
            skArc(sketch, "E328", {"start": v(78.23, 2.13) * mm, "mid": v(78.3, 2.35) * mm, "end": v(78.16, 2.53) * mm});
            skArc(sketch, "E329", {"start": v(78.16, 2.53) * mm, "mid": v(77.23, 2.75) * mm, "end": v(76.3, 2.53) * mm});
            skArc(sketch, "E330", {"start": v(76.3, 2.53) * mm, "mid": v(76.16, 2.35) * mm, "end": v(76.23, 2.13) * mm});
            skLineSegment(sketch, "E331", {"start": v(76.23, 2.13) * mm, "end": v(76.42, 1.93) * mm});
            skArc(sketch, "E332", {"start": v(76.42, 1.57) * mm, "mid": v(76.5, 1.75) * mm, "end": v(76.42, 1.93) * mm});
            skLineSegment(sketch, "E333", {"start": v(76.42, 1.57) * mm, "end": v(76.24, 1.4) * mm});
            skArc(sketch, "E334", {"start": v(75.88, 1.4) * mm, "mid": v(76.06, 1.32) * mm, "end": v(76.24, 1.4) * mm});
            skLineSegment(sketch, "E335", {"start": v(75.88, 1.4) * mm, "end": v(75.69, 1.59) * mm});
            skArc(sketch, "E336", {"start": v(75.69, 1.59) * mm, "mid": v(75.47, 1.66) * mm, "end": v(75.28, 1.52) * mm});
            skArc(sketch, "E337", {"start": v(75.28, 1.52) * mm, "mid": v(75.07, 0.59) * mm, "end": v(75.28, -0.34) * mm});
            skArc(sketch, "E338", {"start": v(75.28, -0.34) * mm, "mid": v(75.47, -0.49) * mm, "end": v(75.69, -0.41) * mm});
            skLineSegment(sketch, "E339", {"start": v(75.69, -0.41) * mm, "end": v(75.88, -0.22) * mm});
            skArc(sketch, "E340", {"start": v(76.24, -0.22) * mm, "mid": v(76.06, -0.15) * mm, "end": v(75.88, -0.22) * mm});
            skLineSegment(sketch, "E341", {"start": v(76.24, -0.22) * mm, "end": v(76.42, -0.4) * mm});
            skArc(sketch, "E342", {"start": v(76.42, -0.76) * mm, "mid": v(76.5, -0.58) * mm, "end": v(76.42, -0.4) * mm});
            skLineSegment(sketch, "E343", {"start": v(76.42, -0.76) * mm, "end": v(76.23, -0.95) * mm});
            skArc(sketch, "E344", {"start": v(76.23, -0.95) * mm, "mid": v(76.16, -1.18) * mm, "end": v(76.3, -1.36) * mm});
            skArc(sketch, "E345", {"start": v(76.3, -1.36) * mm, "mid": v(77.23, -1.57) * mm, "end": v(78.16, -1.36) * mm});
            skArc(sketch, "E346", {"start": v(78.16, -1.36) * mm, "mid": v(78.3, -1.18) * mm, "end": v(78.23, -0.95) * mm});
            skLineSegment(sketch, "E347", {"start": v(78.23, -0.95) * mm, "end": v(78.04, -0.76) * mm});
            skArc(sketch, "E348", {"start": v(78.04, -0.4) * mm, "mid": v(77.96, -0.58) * mm, "end": v(78.04, -0.76) * mm});
            skLineSegment(sketch, "E349", {"start": v(78.04, -0.4) * mm, "end": v(78.22, -0.22) * mm});
            skArc(sketch, "E350", {"start": v(78.58, -0.22) * mm, "mid": v(78.4, -0.15) * mm, "end": v(78.22, -0.22) * mm});
            skLineSegment(sketch, "E351", {"start": v(78.58, -0.22) * mm, "end": v(78.77, -0.41) * mm});
            skArc(sketch, "E352", {"start": v(78.77, -0.41) * mm, "mid": v(79, -0.49) * mm, "end": v(79.18, -0.34) * mm});
            skArc(sketch, "E353", {"start": v(79.18, -0.34) * mm, "mid": v(79.39, 0.59) * mm, "end": v(79.18, 1.52) * mm});
            skArc(sketch, "E354", {"start": v(95.3, 20.4) * mm, "mid": v(95.19, 20.66) * mm, "end": v(94.92, 20.78) * mm});
            skArc(sketch, "E355", {"start": v(94.92, 20.78) * mm, "mid": v(94.64, 20.73) * mm, "end": v(94.48, 20.5) * mm});
            skArc(sketch, "E356", {"start": v(89.05, 18.23) * mm, "mid": v(92.33, 18.01) * mm, "end": v(94.48, 20.5) * mm});
            skArc(sketch, "E357", {"start": v(89.05, 18.23) * mm, "mid": v(88.92, 18.23) * mm, "end": v(88.86, 18.12) * mm});
            skLineSegment(sketch, "E358", {"start": v(88.86, 18.12) * mm, "end": v(88.86, 10.21) * mm});
            skArc(sketch, "E359", {"start": v(88.86, 10.21) * mm, "mid": v(88.9, 10.04) * mm, "end": v(89, 9.9) * mm});
            skArc(sketch, "E360", {"start": v(89.92, 8.08) * mm, "mid": v(89.68, 9.1) * mm, "end": v(89, 9.9) * mm});
            skLineSegment(sketch, "E361", {"start": v(89.92, 8.08) * mm, "end": v(89.92, 4.65) * mm});
            skArc(sketch, "E362", {"start": v(89.92, 4.65) * mm, "mid": v(90.04, 4.38) * mm, "end": v(90.3, 4.27) * mm});
            skLineSegment(sketch, "E363", {"start": v(90.3, 4.27) * mm, "end": v(94.92, 4.27) * mm});
            skArc(sketch, "E364", {"start": v(94.92, 4.27) * mm, "mid": v(95.19, 4.38) * mm, "end": v(95.3, 4.65) * mm});
            skLineSegment(sketch, "E365", {"start": v(95.3, 4.65) * mm, "end": v(95.3, 20.4) * mm});
            skArc(sketch, "E366", {"start": v(92.43, 21.8) * mm, "mid": v(92.25, 21.72) * mm, "end": v(92.18, 21.54) * mm});
            skLineSegment(sketch, "E367", {"start": v(92.43, 21.8) * mm, "end": v(92.7, 21.8) * mm});
            skArc(sketch, "E368", {"start": v(92.7, 21.8) * mm, "mid": v(92.91, 21.9) * mm, "end": v(92.94, 22.13) * mm});
            skArc(sketch, "E369", {"start": v(92.94, 22.13) * mm, "mid": v(92.43, 22.94) * mm, "end": v(91.63, 23.45) * mm});
            skArc(sketch, "E370", {"start": v(91.63, 23.45) * mm, "mid": v(91.4, 23.41) * mm, "end": v(91.29, 23.2) * mm});
            skLineSegment(sketch, "E371", {"start": v(91.29, 23.2) * mm, "end": v(91.29, 22.94) * mm});
            skArc(sketch, "E372", {"start": v(91.03, 22.68) * mm, "mid": v(91.21, 22.76) * mm, "end": v(91.29, 22.94) * mm});
            skLineSegment(sketch, "E373", {"start": v(91.03, 22.68) * mm, "end": v(90.78, 22.68) * mm});
            skArc(sketch, "E374", {"start": v(90.53, 22.94) * mm, "mid": v(90.6, 22.76) * mm, "end": v(90.78, 22.68) * mm});
            skLineSegment(sketch, "E375", {"start": v(90.53, 22.94) * mm, "end": v(90.53, 23.2) * mm});
            skArc(sketch, "E376", {"start": v(90.53, 23.2) * mm, "mid": v(90.42, 23.41) * mm, "end": v(90.19, 23.45) * mm});
            skArc(sketch, "E377", {"start": v(90.19, 23.45) * mm, "mid": v(89.38, 22.94) * mm, "end": v(88.87, 22.13) * mm});
            skArc(sketch, "E378", {"start": v(88.87, 22.13) * mm, "mid": v(88.9, 21.9) * mm, "end": v(89.11, 21.8) * mm});
            skLineSegment(sketch, "E379", {"start": v(89.11, 21.8) * mm, "end": v(89.38, 21.8) * mm});
            skArc(sketch, "E380", {"start": v(89.64, 21.54) * mm, "mid": v(89.56, 21.72) * mm, "end": v(89.38, 21.8) * mm});
            skLineSegment(sketch, "E381", {"start": v(89.64, 21.54) * mm, "end": v(89.64, 21.28) * mm});
            skArc(sketch, "E382", {"start": v(89.38, 21.03) * mm, "mid": v(89.56, 21.1) * mm, "end": v(89.64, 21.28) * mm});
            skLineSegment(sketch, "E383", {"start": v(89.38, 21.03) * mm, "end": v(89.11, 21.03) * mm});
            skArc(sketch, "E384", {"start": v(89.11, 21.03) * mm, "mid": v(88.9, 20.92) * mm, "end": v(88.87, 20.7) * mm});
            skArc(sketch, "E385", {"start": v(88.87, 20.7) * mm, "mid": v(89.38, 19.88) * mm, "end": v(90.19, 19.38) * mm});
            skArc(sketch, "E386", {"start": v(90.19, 19.38) * mm, "mid": v(90.42, 19.4) * mm, "end": v(90.53, 19.62) * mm});
            skLineSegment(sketch, "E387", {"start": v(90.53, 19.62) * mm, "end": v(90.53, 19.89) * mm});
            skArc(sketch, "E388", {"start": v(90.78, 20.14) * mm, "mid": v(90.6, 20.07) * mm, "end": v(90.53, 19.89) * mm});
            skLineSegment(sketch, "E389", {"start": v(90.78, 20.14) * mm, "end": v(91.03, 20.14) * mm});
            skArc(sketch, "E390", {"start": v(91.29, 19.89) * mm, "mid": v(91.21, 20.07) * mm, "end": v(91.03, 20.14) * mm});
            skLineSegment(sketch, "E391", {"start": v(91.29, 19.89) * mm, "end": v(91.29, 19.62) * mm});
            skArc(sketch, "E392", {"start": v(91.29, 19.62) * mm, "mid": v(91.4, 19.4) * mm, "end": v(91.63, 19.38) * mm});
            skArc(sketch, "E393", {"start": v(91.63, 19.38) * mm, "mid": v(92.43, 19.88) * mm, "end": v(92.94, 20.7) * mm});
            skArc(sketch, "E394", {"start": v(92.94, 20.7) * mm, "mid": v(92.91, 20.92) * mm, "end": v(92.7, 21.03) * mm});
            skLineSegment(sketch, "E395", {"start": v(92.7, 21.03) * mm, "end": v(92.43, 21.03) * mm});
            skArc(sketch, "E396", {"start": v(92.18, 21.28) * mm, "mid": v(92.25, 21.1) * mm, "end": v(92.43, 21.03) * mm});
            skLineSegment(sketch, "E397", {"start": v(92.18, 21.28) * mm, "end": v(92.18, 21.54) * mm});
            skArc(sketch, "E398", {"start": v(95.3, 32.5) * mm, "mid": v(95.19, 32.78) * mm, "end": v(94.92, 32.9) * mm});
            skLineSegment(sketch, "E399", {"start": v(94.92, 32.9) * mm, "end": v(88.35, 32.9) * mm});
            skArc(sketch, "E400", {"start": v(88.35, 32.9) * mm, "mid": v(88.22, 32.87) * mm, "end": v(88.1, 32.8) * mm});
            skLineSegment(sketch, "E401", {"start": v(88.1, 32.8) * mm, "end": v(87.37, 32.18) * mm});
            skArc(sketch, "E402", {"start": v(87.37, 32.18) * mm, "mid": v(87.27, 32.05) * mm, "end": v(87.23, 31.89) * mm});
            skLineSegment(sketch, "E403", {"start": v(87.23, 31.89) * mm, "end": v(87.23, 29.89) * mm});
            skArc(sketch, "E404", {"start": v(87.23, 29.89) * mm, "mid": v(87.24, 29.8) * mm, "end": v(87.27, 29.72) * mm});
            skLineSegment(sketch, "E405", {"start": v(87.27, 29.72) * mm, "end": v(88.61, 27.06) * mm});
            skArc(sketch, "E406", {"start": v(88.86, 26.03) * mm, "mid": v(88.8, 26.56) * mm, "end": v(88.61, 27.06) * mm});
            skLineSegment(sketch, "E407", {"start": v(88.86, 26.03) * mm, "end": v(88.86, 25.12) * mm});
            skArc(sketch, "E408", {"start": v(88.86, 25.12) * mm, "mid": v(89.03, 24.8) * mm, "end": v(89.4, 24.77) * mm});
            skArc(sketch, "E409", {"start": v(94.47, 22.33) * mm, "mid": v(92.5, 24.73) * mm, "end": v(89.4, 24.77) * mm});
            skArc(sketch, "E410", {"start": v(94.47, 22.33) * mm, "mid": v(94.6, 22.13) * mm, "end": v(94.84, 22.05) * mm});
            skArc(sketch, "E411", {"start": v(94.84, 22.05) * mm, "mid": v(95.16, 22.13) * mm, "end": v(95.3, 22.43) * mm});
            skLineSegment(sketch, "E412", {"start": v(95.3, 22.43) * mm, "end": v(95.3, 32.5) * mm});
            skArc(sketch, "E413", {"start": v(95.3, 2.36) * mm, "mid": v(95.19, 2.63) * mm, "end": v(94.92, 2.75) * mm});
            skLineSegment(sketch, "E414", {"start": v(94.92, 2.75) * mm, "end": v(88.69, 2.75) * mm});
            skArc(sketch, "E415", {"start": v(88.69, 2.75) * mm, "mid": v(88.42, 2.63) * mm, "end": v(88.3, 2.36) * mm});
            skLineSegment(sketch, "E416", {"start": v(88.3, 2.36) * mm, "end": v(88.3, 0.25) * mm});
            skArc(sketch, "E417", {"start": v(88.3, 0.25) * mm, "mid": v(88.42, -0.02) * mm, "end": v(88.69, -0.13) * mm});
            skLineSegment(sketch, "E418", {"start": v(88.69, -0.13) * mm, "end": v(94.92, -0.13) * mm});
            skArc(sketch, "E419", {"start": v(94.92, -0.13) * mm, "mid": v(95.19, -0.02) * mm, "end": v(95.3, 0.25) * mm});
            skLineSegment(sketch, "E420", {"start": v(95.3, 0.25) * mm, "end": v(95.3, 2.36) * mm});
            skLineSegment(sketch, "E421", {"start": v(96.82, -9.52) * mm, "end": v(-65.62, -9.52) * mm});
            skArc(sketch, "E422", {"start": v(-65.62, -9.52) * mm, "mid": v(-65.88, -9.63) * mm, "end": v(-66, -9.9) * mm});
            skLineSegment(sketch, "E423", {"start": v(-66, -9.9) * mm, "end": v(-66, -34.41) * mm});
            skArc(sketch, "E424", {"start": v(-66.5, -34.92) * mm, "mid": v(-66.14, -34.77) * mm, "end": v(-66, -34.41) * mm});
            skLineSegment(sketch, "E425", {"start": v(-66.5, -34.92) * mm, "end": v(-67.52, -34.92) * mm});
            skArc(sketch, "E426", {"start": v(-68.03, -34.41) * mm, "mid": v(-67.88, -34.77) * mm, "end": v(-67.52, -34.92) * mm});
            skLineSegment(sketch, "E427", {"start": v(-68.03, -34.41) * mm, "end": v(-68.03, -9.9) * mm});
            skArc(sketch, "E428", {"start": v(-68.03, -9.9) * mm, "mid": v(-68.14, -9.63) * mm, "end": v(-68.4, -9.52) * mm});
            skLineSegment(sketch, "E429", {"start": v(-68.4, -9.52) * mm, "end": v(-91.14, -9.52) * mm});
            skArc(sketch, "E430", {"start": v(-91.65, -9.01) * mm, "mid": v(-91.5, -9.37) * mm, "end": v(-91.14, -9.52) * mm});
            skLineSegment(sketch, "E431", {"start": v(-91.65, -9.01) * mm, "end": v(-91.65, -7.55) * mm});
            skArc(sketch, "E432", {"start": v(-89.84, -5.94) * mm, "mid": v(-91.04, -6.4) * mm, "end": v(-91.65, -7.55) * mm});
            skArc(sketch, "E433", {"start": v(-89.47, -6.3) * mm, "mid": v(-89.58, -6.04) * mm, "end": v(-89.84, -5.94) * mm});
            skLineSegment(sketch, "E434", {"start": v(-89.47, -6.3) * mm, "end": v(-89.47, -6.74) * mm});
            skArc(sketch, "E435", {"start": v(-89.47, -6.74) * mm, "mid": v(-89.25, -7.28) * mm, "end": v(-88.71, -7.5) * mm});
            skLineSegment(sketch, "E436", {"start": v(-88.71, -7.5) * mm, "end": v(-83.9, -7.5) * mm});
            skArc(sketch, "E437", {"start": v(-83.9, -7.5) * mm, "mid": v(-83.36, -7.28) * mm, "end": v(-83.14, -6.74) * mm});
            skLineSegment(sketch, "E438", {"start": v(-83.14, -6.74) * mm, "end": v(-83.14, -2.92) * mm});
            skArc(sketch, "E439", {"start": v(-83.14, -2.92) * mm, "mid": v(-83.36, -2.39) * mm, "end": v(-83.9, -2.16) * mm});
            skLineSegment(sketch, "E440", {"start": v(-83.9, -2.16) * mm, "end": v(-88.71, -2.16) * mm});
            skArc(sketch, "E441", {"start": v(-88.71, -2.16) * mm, "mid": v(-89.2, -2.34) * mm, "end": v(-89.46, -2.8) * mm});
            skArc(sketch, "E442", {"start": v(-89.76, -3.05) * mm, "mid": v(-89.57, -2.98) * mm, "end": v(-89.46, -2.8) * mm});
            skLineSegment(sketch, "E443", {"start": v(-89.76, -3.05) * mm, "end": v(-91.13, -3.05) * mm});
            skArc(sketch, "E444", {"start": v(-91.64, -2.54) * mm, "mid": v(-91.49, -2.9) * mm, "end": v(-91.13, -3.05) * mm});
            skLineSegment(sketch, "E445", {"start": v(-91.64, -2.54) * mm, "end": v(-91.64, -2.29) * mm});
            skArc(sketch, "E446", {"start": v(-91.64, -2.29) * mm, "mid": v(-91.71, -2.1) * mm, "end": v(-91.9, -2.04) * mm});
            skLineSegment(sketch, "E447", {"start": v(-91.9, -2.04) * mm, "end": v(-94.92, -2.04) * mm});
            skArc(sketch, "E448", {"start": v(-94.92, -2.04) * mm, "mid": v(-95.03, -2.06) * mm, "end": v(-95.11, -2.12) * mm});
            skArc(sketch, "E449", {"start": v(-95.3, -2.11) * mm, "mid": v(-95.21, -2.16) * mm, "end": v(-95.11, -2.12) * mm});
            skArc(sketch, "E450", {"start": v(-95.3, -2.11) * mm, "mid": v(-95.37, -2.05) * mm, "end": v(-95.44, -2.02) * mm});
            skArc(sketch, "E451", {"start": v(-95.71, -1.65) * mm, "mid": v(-95.64, -1.88) * mm, "end": v(-95.44, -2.02) * mm});
            skLineSegment(sketch, "E452", {"start": v(-95.71, -1.65) * mm, "end": v(-95.71, 4.4) * mm});
            skArc(sketch, "E453", {"start": v(-95.33, 4.78) * mm, "mid": v(-95.6, 4.67) * mm, "end": v(-95.71, 4.4) * mm});
            skLineSegment(sketch, "E454", {"start": v(-95.33, 4.78) * mm, "end": v(-95.02, 4.78) * mm});
            skArc(sketch, "E455", {"start": v(-95.02, 4.78) * mm, "mid": v(-94.75, 4.89) * mm, "end": v(-94.63, 5.16) * mm});
            skLineSegment(sketch, "E456", {"start": v(-94.63, 5.16) * mm, "end": v(-94.63, 8.08) * mm});
            skArc(sketch, "E457", {"start": v(-94.63, 8.08) * mm, "mid": v(-94.73, 8.27) * mm, "end": v(-94.93, 8.33) * mm});
            skLineSegment(sketch, "E458", {"start": v(-94.93, 8.33) * mm, "end": v(-95.46, 8.33) * mm});
            skArc(sketch, "E459", {"start": v(-95.71, 8.58) * mm, "mid": v(-95.64, 8.4) * mm, "end": v(-95.46, 8.33) * mm});
            skLineSegment(sketch, "E460", {"start": v(-95.71, 8.58) * mm, "end": v(-95.71, 23.5) * mm});
            skArc(sketch, "E461", {"start": v(-95.71, 23.5) * mm, "mid": v(-95.75, 23.65) * mm, "end": v(-95.85, 23.78) * mm});
            skLineSegment(sketch, "E462", {"start": v(-95.85, 23.78) * mm, "end": v(-96.79, 24.57) * mm});
            skArc(sketch, "E463", {"start": v(-97.33, 25.73) * mm, "mid": v(-97.19, 25.1) * mm, "end": v(-96.79, 24.57) * mm});
            skLineSegment(sketch, "E464", {"start": v(-97.33, 25.73) * mm, "end": v(-97.33, 32.3) * mm});
            skArc(sketch, "E465", {"start": v(-96.79, 33.47) * mm, "mid": v(-97.19, 32.95) * mm, "end": v(-97.33, 32.3) * mm});
            skLineSegment(sketch, "E466", {"start": v(-96.79, 33.47) * mm, "end": v(-95.27, 34.74) * mm});
            skArc(sketch, "E467", {"start": v(-94.78, 34.92) * mm, "mid": v(-95.04, 34.88) * mm, "end": v(-95.27, 34.74) * mm});
            skLineSegment(sketch, "E468", {"start": v(-94.78, 34.92) * mm, "end": v(-84.53, 34.92) * mm});
            skArc(sketch, "E469", {"start": v(-83.77, 34.16) * mm, "mid": v(-84, 34.7) * mm, "end": v(-84.53, 34.92) * mm});
            skLineSegment(sketch, "E470", {"start": v(-83.77, 34.16) * mm, "end": v(-83.77, 32.5) * mm});
            skArc(sketch, "E471", {"start": v(-84.53, 31.75) * mm, "mid": v(-84, 31.97) * mm, "end": v(-83.77, 32.5) * mm});
            skLineSegment(sketch, "E472", {"start": v(-84.53, 31.75) * mm, "end": v(-84.99, 31.75) * mm});
            skArc(sketch, "E473", {"start": v(-85.3, 32.05) * mm, "mid": v(-85.2, 31.84) * mm, "end": v(-84.99, 31.75) * mm});
            skLineSegment(sketch, "E474", {"start": v(-85.3, 32.05) * mm, "end": v(-85.3, 32.59) * mm});
            skArc(sketch, "E475", {"start": v(-85.3, 32.59) * mm, "mid": v(-85.38, 32.8) * mm, "end": v(-85.6, 32.9) * mm});
            skLineSegment(sketch, "E476", {"start": v(-85.6, 32.9) * mm, "end": v(-86.3, 32.9) * mm});
            skArc(sketch, "E477", {"start": v(-86.3, 32.9) * mm, "mid": v(-86.49, 32.82) * mm, "end": v(-86.56, 32.64) * mm});
            skLineSegment(sketch, "E478", {"start": v(-86.56, 32.64) * mm, "end": v(-86.56, 27.86) * mm});
            skArc(sketch, "E479", {"start": v(-86.56, 27.86) * mm, "mid": v(-86.47, 27.65) * mm, "end": v(-86.26, 27.56) * mm});
            skLineSegment(sketch, "E480", {"start": v(-86.26, 27.56) * mm, "end": v(-85.6, 27.56) * mm});
            skArc(sketch, "E481", {"start": v(-85.6, 27.56) * mm, "mid": v(-85.38, 27.65) * mm, "end": v(-85.3, 27.86) * mm});
            skLineSegment(sketch, "E482", {"start": v(-85.3, 27.86) * mm, "end": v(-85.3, 28.4) * mm});
            skArc(sketch, "E483", {"start": v(-84.99, 28.7) * mm, "mid": v(-85.2, 28.61) * mm, "end": v(-85.3, 28.4) * mm});
            skLineSegment(sketch, "E484", {"start": v(-84.99, 28.7) * mm, "end": v(-84.28, 28.7) * mm});
            skArc(sketch, "E485", {"start": v(-83.77, 28.2) * mm, "mid": v(-83.92, 28.55) * mm, "end": v(-84.28, 28.7) * mm});
            skLineSegment(sketch, "E486", {"start": v(-83.77, 28.2) * mm, "end": v(-83.77, 9.9) * mm});
            skArc(sketch, "E487", {"start": v(-83.77, 9.9) * mm, "mid": v(-83.76, 9.8) * mm, "end": v(-83.72, 9.7) * mm});
            skLineSegment(sketch, "E488", {"start": v(-83.72, 9.7) * mm, "end": v(-83.14, 8.71) * mm});
            skArc(sketch, "E489", {"start": v(-83.36, 8.33) * mm, "mid": v(-83.14, 8.46) * mm, "end": v(-83.14, 8.71) * mm});
            skLineSegment(sketch, "E490", {"start": v(-83.36, 8.33) * mm, "end": v(-83.98, 8.33) * mm});
            skArc(sketch, "E491", {"start": v(-83.98, 8.33) * mm, "mid": v(-84.13, 8.24) * mm, "end": v(-84.19, 8.08) * mm});
            skLineSegment(sketch, "E492", {"start": v(-84.19, 8.08) * mm, "end": v(-84.19, 5.16) * mm});
            skArc(sketch, "E493", {"start": v(-84.19, 5.16) * mm, "mid": v(-84.08, 4.89) * mm, "end": v(-83.8, 4.78) * mm});
            skLineSegment(sketch, "E494", {"start": v(-83.8, 4.78) * mm, "end": v(-34.17, 4.78) * mm});
            skArc(sketch, "E495", {"start": v(-34.17, 4.78) * mm, "mid": v(-33.9, 4.89) * mm, "end": v(-33.8, 5.16) * mm});
            skLineSegment(sketch, "E496", {"start": v(-33.8, 5.16) * mm, "end": v(-33.8, 8.08) * mm});
            skArc(sketch, "E497", {"start": v(-33.8, 8.08) * mm, "mid": v(-33.88, 8.27) * mm, "end": v(-34.1, 8.33) * mm});
            skLineSegment(sketch, "E498", {"start": v(-34.1, 8.33) * mm, "end": v(-34.62, 8.33) * mm});
            skArc(sketch, "E499", {"start": v(-34.87, 8.58) * mm, "mid": v(-34.8, 8.4) * mm, "end": v(-34.62, 8.33) * mm});
            skLineSegment(sketch, "E500", {"start": v(-34.87, 8.58) * mm, "end": v(-34.87, 23.5) * mm});
            skArc(sketch, "E501", {"start": v(-34.87, 23.5) * mm, "mid": v(-34.9, 23.65) * mm, "end": v(-35, 23.78) * mm});
            skLineSegment(sketch, "E502", {"start": v(-35, 23.78) * mm, "end": v(-35.94, 24.57) * mm});
            skArc(sketch, "E503", {"start": v(-36.49, 25.73) * mm, "mid": v(-36.34, 25.1) * mm, "end": v(-35.94, 24.57) * mm});
            skLineSegment(sketch, "E504", {"start": v(-36.49, 25.73) * mm, "end": v(-36.49, 32.3) * mm});
            skArc(sketch, "E505", {"start": v(-35.94, 33.47) * mm, "mid": v(-36.34, 32.95) * mm, "end": v(-36.49, 32.3) * mm});
            skLineSegment(sketch, "E506", {"start": v(-35.94, 33.47) * mm, "end": v(-34.42, 34.74) * mm});
            skArc(sketch, "E507", {"start": v(-33.93, 34.92) * mm, "mid": v(-34.2, 34.88) * mm, "end": v(-34.42, 34.74) * mm});
            skLineSegment(sketch, "E508", {"start": v(-33.93, 34.92) * mm, "end": v(-23.69, 34.92) * mm});
            skArc(sketch, "E509", {"start": v(-22.93, 34.16) * mm, "mid": v(-23.15, 34.7) * mm, "end": v(-23.69, 34.92) * mm});
            skLineSegment(sketch, "E510", {"start": v(-22.93, 34.16) * mm, "end": v(-22.93, 32.5) * mm});
            skArc(sketch, "E511", {"start": v(-23.69, 31.75) * mm, "mid": v(-23.15, 31.97) * mm, "end": v(-22.93, 32.5) * mm});
            skLineSegment(sketch, "E512", {"start": v(-23.69, 31.75) * mm, "end": v(-24.14, 31.75) * mm});
            skArc(sketch, "E513", {"start": v(-24.45, 32.05) * mm, "mid": v(-24.36, 31.84) * mm, "end": v(-24.14, 31.75) * mm});
            skLineSegment(sketch, "E514", {"start": v(-24.45, 32.05) * mm, "end": v(-24.45, 32.59) * mm});
            skArc(sketch, "E515", {"start": v(-24.45, 32.59) * mm, "mid": v(-24.54, 32.8) * mm, "end": v(-24.75, 32.9) * mm});
            skLineSegment(sketch, "E516", {"start": v(-24.75, 32.9) * mm, "end": v(-25.47, 32.9) * mm});
            skArc(sketch, "E517", {"start": v(-25.47, 32.9) * mm, "mid": v(-25.64, 32.82) * mm, "end": v(-25.72, 32.64) * mm});
            skLineSegment(sketch, "E518", {"start": v(-25.72, 32.64) * mm, "end": v(-25.72, 27.86) * mm});
            skArc(sketch, "E519", {"start": v(-25.72, 27.86) * mm, "mid": v(-25.63, 27.65) * mm, "end": v(-25.41, 27.56) * mm});
            skLineSegment(sketch, "E520", {"start": v(-25.41, 27.56) * mm, "end": v(-24.75, 27.56) * mm});
            skArc(sketch, "E521", {"start": v(-24.75, 27.56) * mm, "mid": v(-24.54, 27.65) * mm, "end": v(-24.45, 27.86) * mm});
            skLineSegment(sketch, "E522", {"start": v(-24.45, 27.86) * mm, "end": v(-24.45, 28.4) * mm});
            skArc(sketch, "E523", {"start": v(-24.14, 28.7) * mm, "mid": v(-24.36, 28.61) * mm, "end": v(-24.45, 28.4) * mm});
            skLineSegment(sketch, "E524", {"start": v(-24.14, 28.7) * mm, "end": v(-23.43, 28.7) * mm});
            skArc(sketch, "E525", {"start": v(-22.93, 28.2) * mm, "mid": v(-23.07, 28.55) * mm, "end": v(-23.43, 28.7) * mm});
            skLineSegment(sketch, "E526", {"start": v(-22.93, 28.2) * mm, "end": v(-22.93, 9.9) * mm});
            skArc(sketch, "E527", {"start": v(-22.93, 9.9) * mm, "mid": v(-22.91, 9.8) * mm, "end": v(-22.87, 9.7) * mm});
            skLineSegment(sketch, "E528", {"start": v(-22.87, 9.7) * mm, "end": v(-22.3, 8.71) * mm});
            skArc(sketch, "E529", {"start": v(-22.52, 8.33) * mm, "mid": v(-22.3, 8.46) * mm, "end": v(-22.3, 8.71) * mm});
            skLineSegment(sketch, "E530", {"start": v(-22.52, 8.33) * mm, "end": v(-23.1, 8.33) * mm});
            skArc(sketch, "E531", {"start": v(-23.1, 8.33) * mm, "mid": v(-23.27, 8.25) * mm, "end": v(-23.34, 8.08) * mm});
            skLineSegment(sketch, "E532", {"start": v(-23.34, 8.08) * mm, "end": v(-23.34, 5.16) * mm});
            skArc(sketch, "E533", {"start": v(-23.34, 5.16) * mm, "mid": v(-23.23, 4.89) * mm, "end": v(-22.96, 4.78) * mm});
            skLineSegment(sketch, "E534", {"start": v(-22.96, 4.78) * mm, "end": v(26.67, 4.78) * mm});
            skArc(sketch, "E535", {"start": v(26.67, 4.78) * mm, "mid": v(26.94, 4.89) * mm, "end": v(27.05, 5.16) * mm});
            skLineSegment(sketch, "E536", {"start": v(27.05, 5.16) * mm, "end": v(27.05, 8.08) * mm});
            skArc(sketch, "E537", {"start": v(27.05, 8.08) * mm, "mid": v(26.96, 8.27) * mm, "end": v(26.75, 8.33) * mm});
            skLineSegment(sketch, "E538", {"start": v(26.75, 8.33) * mm, "end": v(26.23, 8.33) * mm});
            skArc(sketch, "E539", {"start": v(25.97, 8.58) * mm, "mid": v(26.05, 8.4) * mm, "end": v(26.23, 8.33) * mm});
            skLineSegment(sketch, "E540", {"start": v(25.97, 8.58) * mm, "end": v(25.97, 23.5) * mm});
            skArc(sketch, "E541", {"start": v(25.97, 23.5) * mm, "mid": v(25.94, 23.65) * mm, "end": v(25.84, 23.78) * mm});
            skLineSegment(sketch, "E542", {"start": v(25.84, 23.78) * mm, "end": v(24.9, 24.57) * mm});
            skArc(sketch, "E543", {"start": v(24.36, 25.73) * mm, "mid": v(24.5, 25.1) * mm, "end": v(24.9, 24.57) * mm});
            skLineSegment(sketch, "E544", {"start": v(24.36, 25.73) * mm, "end": v(24.36, 32.3) * mm});
            skArc(sketch, "E545", {"start": v(24.9, 33.47) * mm, "mid": v(24.5, 32.95) * mm, "end": v(24.36, 32.3) * mm});
            skLineSegment(sketch, "E546", {"start": v(24.9, 33.47) * mm, "end": v(26.42, 34.74) * mm});
            skArc(sketch, "E547", {"start": v(26.9, 34.92) * mm, "mid": v(26.65, 34.88) * mm, "end": v(26.42, 34.74) * mm});
            skLineSegment(sketch, "E548", {"start": v(26.9, 34.92) * mm, "end": v(37.16, 34.92) * mm});
            skArc(sketch, "E549", {"start": v(37.92, 34.16) * mm, "mid": v(37.7, 34.7) * mm, "end": v(37.16, 34.92) * mm});
            skLineSegment(sketch, "E550", {"start": v(37.92, 34.16) * mm, "end": v(37.92, 32.5) * mm});
            skArc(sketch, "E551", {"start": v(37.16, 31.75) * mm, "mid": v(37.7, 31.97) * mm, "end": v(37.92, 32.5) * mm});
            skLineSegment(sketch, "E552", {"start": v(37.16, 31.75) * mm, "end": v(36.7, 31.75) * mm});
            skArc(sketch, "E553", {"start": v(36.4, 32.05) * mm, "mid": v(36.48, 31.84) * mm, "end": v(36.7, 31.75) * mm});
            skLineSegment(sketch, "E554", {"start": v(36.4, 32.05) * mm, "end": v(36.4, 32.59) * mm});
            skArc(sketch, "E555", {"start": v(36.4, 32.59) * mm, "mid": v(36.3, 32.8) * mm, "end": v(36.09, 32.9) * mm});
            skLineSegment(sketch, "E556", {"start": v(36.09, 32.9) * mm, "end": v(35.38, 32.9) * mm});
            skArc(sketch, "E557", {"start": v(35.38, 32.9) * mm, "mid": v(35.2, 32.82) * mm, "end": v(35.12, 32.64) * mm});
            skLineSegment(sketch, "E558", {"start": v(35.12, 32.64) * mm, "end": v(35.12, 27.86) * mm});
            skArc(sketch, "E559", {"start": v(35.12, 27.86) * mm, "mid": v(35.21, 27.65) * mm, "end": v(35.43, 27.56) * mm});
            skLineSegment(sketch, "E560", {"start": v(35.43, 27.56) * mm, "end": v(36.09, 27.56) * mm});
            skArc(sketch, "E561", {"start": v(36.09, 27.56) * mm, "mid": v(36.3, 27.65) * mm, "end": v(36.4, 27.86) * mm});
            skLineSegment(sketch, "E562", {"start": v(36.4, 27.86) * mm, "end": v(36.4, 28.4) * mm});
            skArc(sketch, "E563", {"start": v(36.7, 28.7) * mm, "mid": v(36.48, 28.61) * mm, "end": v(36.4, 28.4) * mm});
            skLineSegment(sketch, "E564", {"start": v(36.7, 28.7) * mm, "end": v(37.4, 28.7) * mm});
            skArc(sketch, "E565", {"start": v(37.92, 28.2) * mm, "mid": v(37.77, 28.55) * mm, "end": v(37.4, 28.7) * mm});
            skLineSegment(sketch, "E566", {"start": v(37.92, 28.2) * mm, "end": v(37.92, 9.9) * mm});
            skArc(sketch, "E567", {"start": v(37.92, 9.9) * mm, "mid": v(37.93, 9.8) * mm, "end": v(37.97, 9.7) * mm});
            skLineSegment(sketch, "E568", {"start": v(37.97, 9.7) * mm, "end": v(38.54, 8.71) * mm});
            skArc(sketch, "E569", {"start": v(38.32, 8.33) * mm, "mid": v(38.54, 8.46) * mm, "end": v(38.54, 8.71) * mm});
            skLineSegment(sketch, "E570", {"start": v(38.32, 8.33) * mm, "end": v(37.75, 8.33) * mm});
            skArc(sketch, "E571", {"start": v(37.75, 8.33) * mm, "mid": v(37.57, 8.26) * mm, "end": v(37.5, 8.08) * mm});
            skLineSegment(sketch, "E572", {"start": v(37.5, 8.08) * mm, "end": v(37.5, 5.16) * mm});
            skArc(sketch, "E573", {"start": v(37.5, 5.16) * mm, "mid": v(37.61, 4.89) * mm, "end": v(37.88, 4.78) * mm});
            skLineSegment(sketch, "E574", {"start": v(37.88, 4.78) * mm, "end": v(87.51, 4.78) * mm});
            skArc(sketch, "E575", {"start": v(87.51, 4.78) * mm, "mid": v(87.78, 4.89) * mm, "end": v(87.9, 5.16) * mm});
            skLineSegment(sketch, "E576", {"start": v(87.9, 5.16) * mm, "end": v(87.9, 8.08) * mm});
            skArc(sketch, "E577", {"start": v(87.9, 8.08) * mm, "mid": v(87.82, 8.26) * mm, "end": v(87.64, 8.33) * mm});
            skLineSegment(sketch, "E578", {"start": v(87.64, 8.33) * mm, "end": v(87.08, 8.33) * mm});
            skArc(sketch, "E579", {"start": v(86.82, 8.59) * mm, "mid": v(86.9, 8.4) * mm, "end": v(87.08, 8.33) * mm});
            skLineSegment(sketch, "E580", {"start": v(86.82, 8.59) * mm, "end": v(86.82, 26) * mm});
            skArc(sketch, "E581", {"start": v(86.82, 26) * mm, "mid": v(86.81, 26.09) * mm, "end": v(86.78, 26.17) * mm});
            skLineSegment(sketch, "E582", {"start": v(86.78, 26.17) * mm, "end": v(85.44, 28.83) * mm});
            skArc(sketch, "E583", {"start": v(85.2, 29.86) * mm, "mid": v(85.26, 29.33) * mm, "end": v(85.44, 28.83) * mm});
            skLineSegment(sketch, "E584", {"start": v(85.2, 29.86) * mm, "end": v(85.2, 32.3) * mm});
            skArc(sketch, "E585", {"start": v(85.74, 33.47) * mm, "mid": v(85.34, 32.95) * mm, "end": v(85.2, 32.3) * mm});
            skLineSegment(sketch, "E586", {"start": v(85.74, 33.47) * mm, "end": v(87.26, 34.74) * mm});
            skArc(sketch, "E587", {"start": v(87.75, 34.92) * mm, "mid": v(87.5, 34.88) * mm, "end": v(87.26, 34.74) * mm});
            skLineSegment(sketch, "E588", {"start": v(87.75, 34.92) * mm, "end": v(96.31, 34.92) * mm});
            skArc(sketch, "E589", {"start": v(97.33, 33.9) * mm, "mid": v(97.03, 34.63) * mm, "end": v(96.31, 34.92) * mm});
            skLineSegment(sketch, "E590", {"start": v(97.33, 33.9) * mm, "end": v(97.33, -2.54) * mm});
            skArc(sketch, "E591", {"start": v(96.82, -3.05) * mm, "mid": v(97.18, -2.9) * mm, "end": v(97.33, -2.54) * mm});
            skLineSegment(sketch, "E592", {"start": v(96.82, -3.05) * mm, "end": v(95.44, -3.05) * mm});
            skArc(sketch, "E593", {"start": v(95.14, -2.8) * mm, "mid": v(95.25, -2.98) * mm, "end": v(95.44, -3.05) * mm});
            skArc(sketch, "E594", {"start": v(95.14, -2.8) * mm, "mid": v(94.88, -2.34) * mm, "end": v(94.4, -2.16) * mm});
            skLineSegment(sketch, "E595", {"start": v(94.4, -2.16) * mm, "end": v(89.58, -2.16) * mm});
            skArc(sketch, "E596", {"start": v(89.58, -2.16) * mm, "mid": v(89.04, -2.39) * mm, "end": v(88.82, -2.92) * mm});
            skLineSegment(sketch, "E597", {"start": v(88.82, -2.92) * mm, "end": v(88.82, -6.74) * mm});
            skArc(sketch, "E598", {"start": v(88.82, -6.74) * mm, "mid": v(89.04, -7.28) * mm, "end": v(89.58, -7.5) * mm});
            skLineSegment(sketch, "E599", {"start": v(89.58, -7.5) * mm, "end": v(94.4, -7.5) * mm});
            skArc(sketch, "E600", {"start": v(94.4, -7.5) * mm, "mid": v(94.93, -7.28) * mm, "end": v(95.15, -6.74) * mm});
            skLineSegment(sketch, "E601", {"start": v(95.15, -6.74) * mm, "end": v(95.15, -6.3) * mm});
            skArc(sketch, "E602", {"start": v(95.52, -5.94) * mm, "mid": v(95.26, -6.04) * mm, "end": v(95.15, -6.3) * mm});
            skArc(sketch, "E603", {"start": v(97.33, -7.55) * mm, "mid": v(96.72, -6.4) * mm, "end": v(95.52, -5.94) * mm});
            skLineSegment(sketch, "E604", {"start": v(97.33, -7.55) * mm, "end": v(97.33, -9.01) * mm});
            skArc(sketch, "E605", {"start": v(96.82, -9.52) * mm, "mid": v(97.18, -9.37) * mm, "end": v(97.33, -9.01) * mm});
            skLineSegment(sketch, "E606", {"start": v(-25.76, 4.27) * mm, "end": v(-31.38, 4.27) * mm});
            skArc(sketch, "E607", {"start": v(-31.76, 4.65) * mm, "mid": v(-31.65, 4.38) * mm, "end": v(-31.38, 4.27) * mm});
            skLineSegment(sketch, "E608", {"start": v(-31.76, 4.65) * mm, "end": v(-31.76, 8.08) * mm});
            skArc(sketch, "E609", {"start": v(-31.76, 8.08) * mm, "mid": v(-32, 9.1) * mm, "end": v(-32.68, 9.92) * mm});
            skArc(sketch, "E610", {"start": v(-32.84, 10.22) * mm, "mid": v(-32.8, 10.05) * mm, "end": v(-32.68, 9.92) * mm});
            skLineSegment(sketch, "E611", {"start": v(-32.84, 10.22) * mm, "end": v(-32.84, 18.35) * mm});
            skArc(sketch, "E612", {"start": v(-32.65, 18.46) * mm, "mid": v(-32.78, 18.46) * mm, "end": v(-32.84, 18.35) * mm});
            skArc(sketch, "E613", {"start": v(-32.65, 18.46) * mm, "mid": v(-29.37, 18.24) * mm, "end": v(-27.22, 20.71) * mm});
            skArc(sketch, "E614", {"start": v(-26.85, 21) * mm, "mid": v(-27.09, 20.92) * mm, "end": v(-27.22, 20.71) * mm});
            skLineSegment(sketch, "E615", {"start": v(-26.85, 21) * mm, "end": v(-25.34, 21) * mm});
            skArc(sketch, "E616", {"start": v(-24.96, 20.62) * mm, "mid": v(-25.07, 20.89) * mm, "end": v(-25.34, 21) * mm});
            skLineSegment(sketch, "E617", {"start": v(-24.96, 20.62) * mm, "end": v(-24.96, 9.51) * mm});
            skArc(sketch, "E618", {"start": v(-25.02, 9.3) * mm, "mid": v(-24.97, 9.4) * mm, "end": v(-24.96, 9.51) * mm});
            skArc(sketch, "E619", {"start": v(-25.02, 9.3) * mm, "mid": v(-25.28, 8.72) * mm, "end": v(-25.38, 8.08) * mm});
            skLineSegment(sketch, "E620", {"start": v(-25.38, 8.08) * mm, "end": v(-25.38, 4.65) * mm});
            skArc(sketch, "E621", {"start": v(-25.76, 4.27) * mm, "mid": v(-25.49, 4.38) * mm, "end": v(-25.38, 4.65) * mm});
            skLineSegment(sketch, "E622", {"start": v(-25.34, 22.27) * mm, "end": v(-26.85, 22.27) * mm});
            skArc(sketch, "E623", {"start": v(-27.22, 22.56) * mm, "mid": v(-27.09, 22.35) * mm, "end": v(-26.85, 22.27) * mm});
            skArc(sketch, "E624", {"start": v(-27.22, 22.56) * mm, "mid": v(-29.54, 25.1) * mm, "end": v(-32.94, 24.62) * mm});
            skArc(sketch, "E625", {"start": v(-33.13, 24.66) * mm, "mid": v(-33.05, 24.6) * mm, "end": v(-32.94, 24.62) * mm});
            skArc(sketch, "E626", {"start": v(-33.13, 24.66) * mm, "mid": v(-33.36, 25) * mm, "end": v(-33.66, 25.3) * mm});
            skLineSegment(sketch, "E627", {"start": v(-33.66, 25.3) * mm, "end": v(-34.32, 25.86) * mm});
            skArc(sketch, "E628", {"start": v(-34.45, 26.15) * mm, "mid": v(-34.42, 25.99) * mm, "end": v(-34.32, 25.86) * mm});
            skLineSegment(sketch, "E629", {"start": v(-34.45, 26.15) * mm, "end": v(-34.45, 31.89) * mm});
            skArc(sketch, "E630", {"start": v(-34.32, 32.18) * mm, "mid": v(-34.42, 32.05) * mm, "end": v(-34.45, 31.89) * mm});
            skLineSegment(sketch, "E631", {"start": v(-34.32, 32.18) * mm, "end": v(-33.58, 32.8) * mm});
            skArc(sketch, "E632", {"start": v(-33.33, 32.9) * mm, "mid": v(-33.46, 32.87) * mm, "end": v(-33.58, 32.8) * mm});
            skLineSegment(sketch, "E633", {"start": v(-33.33, 32.9) * mm, "end": v(-28.13, 32.9) * mm});
            skArc(sketch, "E634", {"start": v(-27.75, 32.5) * mm, "mid": v(-27.86, 32.78) * mm, "end": v(-28.13, 32.9) * mm});
            skLineSegment(sketch, "E635", {"start": v(-27.75, 32.5) * mm, "end": v(-27.75, 27.81) * mm});
            skArc(sketch, "E636", {"start": v(-27.75, 27.81) * mm, "mid": v(-27.08, 26.2) * mm, "end": v(-25.47, 25.52) * mm});
            skLineSegment(sketch, "E637", {"start": v(-25.47, 25.52) * mm, "end": v(-25.34, 25.52) * mm});
            skArc(sketch, "E638", {"start": v(-24.96, 25.14) * mm, "mid": v(-25.07, 25.41) * mm, "end": v(-25.34, 25.52) * mm});
            skLineSegment(sketch, "E639", {"start": v(-24.96, 25.14) * mm, "end": v(-24.96, 22.65) * mm});
            skArc(sketch, "E640", {"start": v(-25.34, 22.27) * mm, "mid": v(-25.07, 22.38) * mm, "end": v(-24.96, 22.65) * mm});
            skArc(sketch, "E641", {"start": v(-30.4, 19.84) * mm, "mid": v(-30.3, 19.63) * mm, "end": v(-30.07, 19.6) * mm});
            skLineSegment(sketch, "E642", {"start": v(-30.4, 19.84) * mm, "end": v(-30.4, 20.11) * mm});
            skArc(sketch, "E643", {"start": v(-30.4, 20.11) * mm, "mid": v(-30.48, 20.3) * mm, "end": v(-30.66, 20.37) * mm});
            skLineSegment(sketch, "E644", {"start": v(-30.66, 20.37) * mm, "end": v(-30.92, 20.37) * mm});
            skArc(sketch, "E645", {"start": v(-30.92, 20.37) * mm, "mid": v(-31.1, 20.3) * mm, "end": v(-31.17, 20.11) * mm});
            skLineSegment(sketch, "E646", {"start": v(-31.17, 20.11) * mm, "end": v(-31.17, 19.84) * mm});
            skArc(sketch, "E647", {"start": v(-31.5, 19.6) * mm, "mid": v(-31.28, 19.63) * mm, "end": v(-31.17, 19.84) * mm});
            skArc(sketch, "E648", {"start": v(-32.82, 20.92) * mm, "mid": v(-32.32, 20.1) * mm, "end": v(-31.5, 19.6) * mm});
            skArc(sketch, "E649", {"start": v(-32.59, 21.25) * mm, "mid": v(-32.8, 21.15) * mm, "end": v(-32.82, 20.92) * mm});
            skLineSegment(sketch, "E650", {"start": v(-32.59, 21.25) * mm, "end": v(-32.31, 21.25) * mm});
            skArc(sketch, "E651", {"start": v(-32.31, 21.25) * mm, "mid": v(-32.13, 21.33) * mm, "end": v(-32.06, 21.5) * mm});
            skLineSegment(sketch, "E652", {"start": v(-32.06, 21.5) * mm, "end": v(-32.06, 21.76) * mm});
            skArc(sketch, "E653", {"start": v(-32.06, 21.76) * mm, "mid": v(-32.13, 21.94) * mm, "end": v(-32.31, 22.02) * mm});
            skLineSegment(sketch, "E654", {"start": v(-32.31, 22.02) * mm, "end": v(-32.59, 22.02) * mm});
            skArc(sketch, "E655", {"start": v(-32.82, 22.35) * mm, "mid": v(-32.8, 22.12) * mm, "end": v(-32.59, 22.02) * mm});
            skArc(sketch, "E656", {"start": v(-31.5, 23.67) * mm, "mid": v(-32.32, 23.16) * mm, "end": v(-32.82, 22.35) * mm});
            skArc(sketch, "E657", {"start": v(-31.17, 23.43) * mm, "mid": v(-31.28, 23.64) * mm, "end": v(-31.5, 23.67) * mm});
            skLineSegment(sketch, "E658", {"start": v(-31.17, 23.43) * mm, "end": v(-31.17, 23.16) * mm});
            skArc(sketch, "E659", {"start": v(-31.17, 23.16) * mm, "mid": v(-31.1, 22.98) * mm, "end": v(-30.92, 22.9) * mm});
            skLineSegment(sketch, "E660", {"start": v(-30.92, 22.9) * mm, "end": v(-30.66, 22.9) * mm});
            skArc(sketch, "E661", {"start": v(-30.66, 22.9) * mm, "mid": v(-30.48, 22.98) * mm, "end": v(-30.4, 23.16) * mm});
            skLineSegment(sketch, "E662", {"start": v(-30.4, 23.16) * mm, "end": v(-30.4, 23.43) * mm});
            skArc(sketch, "E663", {"start": v(-30.07, 23.67) * mm, "mid": v(-30.3, 23.64) * mm, "end": v(-30.4, 23.43) * mm});
            skArc(sketch, "E664", {"start": v(-28.75, 22.35) * mm, "mid": v(-29.26, 23.16) * mm, "end": v(-30.07, 23.67) * mm});
            skArc(sketch, "E665", {"start": v(-29, 22.02) * mm, "mid": v(-28.79, 22.12) * mm, "end": v(-28.75, 22.35) * mm});
            skLineSegment(sketch, "E666", {"start": v(-29, 22.02) * mm, "end": v(-29.27, 22.02) * mm});
            skArc(sketch, "E667", {"start": v(-29.27, 22.02) * mm, "mid": v(-29.44, 21.94) * mm, "end": v(-29.52, 21.76) * mm});
            skLineSegment(sketch, "E668", {"start": v(-29.52, 21.76) * mm, "end": v(-29.52, 21.5) * mm});
            skArc(sketch, "E669", {"start": v(-29.52, 21.5) * mm, "mid": v(-29.44, 21.33) * mm, "end": v(-29.27, 21.25) * mm});
            skLineSegment(sketch, "E670", {"start": v(-29.27, 21.25) * mm, "end": v(-29, 21.25) * mm});
            skArc(sketch, "E671", {"start": v(-28.75, 20.92) * mm, "mid": v(-28.79, 21.15) * mm, "end": v(-29, 21.25) * mm});
            skArc(sketch, "E672", {"start": v(-30.07, 19.6) * mm, "mid": v(-29.26, 20.1) * mm, "end": v(-28.75, 20.92) * mm});
            skSolve(sketch);
        }
        {
            var Q0;
            Q0=makeQuery(id+"F0.imprint","IMPRINT",FACE,{"disambiguationData":[TD([[makeQuery(id+"F0.imprint","IMPRINT",EDGE,{"derivedFrom":sQuery(id+"F0.wireOp",EDGE,"E310")}),1.0]])]});
            var Q1;
            Q1=makeQuery(id+"F0.imprint","IMPRINT",FACE,{"disambiguationData":[TD([[makeQuery(id+"F0.imprint","IMPRINT",EDGE,{"derivedFrom":sQuery(id+"F0.wireOp",EDGE,"E354")}),1.0]])]});
            var Q2;
            Q2=makeQuery(id+"F0.imprint","IMPRINT",FACE,{"disambiguationData":[TD([[makeQuery(id+"F0.imprint","IMPRINT",EDGE,{"derivedFrom":sQuery(id+"F0.wireOp",EDGE,"E398")}),1.0]])]});
            var Q3;
            Q3=makeQuery(id+"F0.imprint","IMPRINT",FACE,{"disambiguationData":[TD([[makeQuery(id+"F0.imprint","IMPRINT",EDGE,{"derivedFrom":sQuery(id+"F0.wireOp",EDGE,"E413")}),1.0]])]});
            var Q4;
            Q4=makeQuery(id+"F0.imprint","IMPRINT",FACE,{"disambiguationData":[TD([[makeQuery(id+"F0.imprint","IMPRINT",EDGE,{"derivedFrom":sQuery(id+"F0.wireOp",EDGE,"E606")}),-1.0]])]});
            var Q5;
            Q5=makeQuery(id+"F0.imprint","IMPRINT",FACE,{"disambiguationData":[TD([[makeQuery(id+"F0.imprint","IMPRINT",EDGE,{"derivedFrom":sQuery(id+"F0.wireOp",EDGE,"E622")}),-1.0]])]});
            var Q6;
            Q6=makeQuery(id+"F0.imprint","IMPRINT",FACE,{"disambiguationData":[TD([[makeQuery(id+"F0.imprint","IMPRINT",EDGE,{"derivedFrom":sQuery(id+"F0.wireOp",EDGE,"E302")}),1.0]])]});
            var Q7;
            Q7=makeQuery(id+"F0.imprint","IMPRINT",FACE,{"disambiguationData":[TD([[makeQuery(id+"F0.imprint","IMPRINT",EDGE,{"derivedFrom":sQuery(id+"F0.wireOp",EDGE,"E282")}),1.0]])]});
            var Q8;
            Q8=makeQuery(id+"F0.imprint","IMPRINT",FACE,{"disambiguationData":[TD([[makeQuery(id+"F0.imprint","IMPRINT",EDGE,{"derivedFrom":sQuery(id+"F0.wireOp",EDGE,"E290")}),1.0]])]});
            var Q9;
            Q9=makeQuery(id+"F0.imprint","IMPRINT",FACE,{"disambiguationData":[TD([[makeQuery(id+"F0.imprint","IMPRINT",EDGE,{"derivedFrom":sQuery(id+"F0.wireOp",EDGE,"E0")}),1.0]])]});
            var Q10;
            Q10=makeQuery(id+"F0.imprint","IMPRINT",FACE,{"disambiguationData":[TD([[makeQuery(id+"F0.imprint","IMPRINT",EDGE,{"derivedFrom":sQuery(id+"F0.wireOp",EDGE,"E8")}),1.0]])]});
            var Q11;
            Q11=makeQuery(id+"F0.imprint","IMPRINT",FACE,{"disambiguationData":[TD([[makeQuery(id+"F0.imprint","IMPRINT",EDGE,{"derivedFrom":sQuery(id+"F0.wireOp",EDGE,"E52")}),1.0]])]});
            var Q12;
            Q12=makeQuery(id+"F0.imprint","IMPRINT",FACE,{"disambiguationData":[TD([[makeQuery(id+"F0.imprint","IMPRINT",EDGE,{"derivedFrom":sQuery(id+"F0.wireOp",EDGE,"E60")}),1.0]])]});
            var Q13;
            Q13=makeQuery(id+"F0.imprint","IMPRINT",FACE,{"disambiguationData":[TD([[makeQuery(id+"F0.imprint","IMPRINT",EDGE,{"derivedFrom":sQuery(id+"F0.wireOp",EDGE,"E68")}),1.0]])]});
            var Q14;
            Q14=makeQuery(id+"F0.imprint","IMPRINT",FACE,{"disambiguationData":[TD([[makeQuery(id+"F0.imprint","IMPRINT",EDGE,{"derivedFrom":sQuery(id+"F0.wireOp",EDGE,"E110")}),1.0]])]});
            var Q15;
            Q15=makeQuery(id+"F0.imprint","IMPRINT",FACE,{"disambiguationData":[TD([[makeQuery(id+"F0.imprint","IMPRINT",EDGE,{"derivedFrom":sQuery(id+"F0.wireOp",EDGE,"E118")}),1.0]])]});
            var Q16;
            Q16=makeQuery(id+"F0.imprint","IMPRINT",FACE,{"disambiguationData":[TD([[makeQuery(id+"F0.imprint","IMPRINT",EDGE,{"derivedFrom":sQuery(id+"F0.wireOp",EDGE,"E184")}),1.0]])]});
            var Q17;
            Q17=makeQuery(id+"F0.imprint","IMPRINT",FACE,{"disambiguationData":[TD([[makeQuery(id+"F0.imprint","IMPRINT",EDGE,{"derivedFrom":sQuery(id+"F0.wireOp",EDGE,"E218")}),1.0]])]});
            var Q18;
            Q18=makeQuery(id+"F0.imprint","IMPRINT",FACE,{"disambiguationData":[TD([[makeQuery(id+"F0.imprint","IMPRINT",EDGE,{"derivedFrom":sQuery(id+"F0.wireOp",EDGE,"E322")}),1.0]])]});
            var Q19;
            Q19=makeQuery(id+"F0.imprint","IMPRINT",FACE,{"disambiguationData":[TD([[makeQuery(id+"F0.imprint","IMPRINT",EDGE,{"derivedFrom":sQuery(id+"F0.wireOp",EDGE,"E152")}),-1.0]])]});
            var Q20;
            Q20=makeQuery(id+"F0.imprint","IMPRINT",FACE,{"disambiguationData":[TD([[makeQuery(id+"F0.imprint","IMPRINT",EDGE,{"derivedFrom":sQuery(id+"F0.wireOp",EDGE,"E250")}),1.0]])]});
            var Q21;
            Q21=makeQuery(id+"F0.imprint","IMPRINT",FACE,{"disambiguationData":[TD([[makeQuery(id+"F0.imprint","IMPRINT",EDGE,{"derivedFrom":sQuery(id+"F0.wireOp",EDGE,"E366")}),-1.0]])]});
            var Q22;
            Q22=makeQuery(id+"F0.imprint","IMPRINT",FACE,{"disambiguationData":[TD([[makeQuery(id+"F0.imprint","IMPRINT",EDGE,{"derivedFrom":sQuery(id+"F0.wireOp",EDGE,"E641")}),1.0]])]});
            var Q23;
            Q23=makeQuery(id+"F0.imprint","IMPRINT",FACE,{"disambiguationData":[TD([[makeQuery(id+"F0.imprint","IMPRINT",EDGE,{"derivedFrom":sQuery(id+"F0.wireOp",EDGE,"E78")}),1.0]])]});
            var Q24;
            Q24=makeQuery(id+"F0.imprint","IMPRINT",FACE,{"disambiguationData":[TD([[makeQuery(id+"F0.imprint","IMPRINT",EDGE,{"derivedFrom":sQuery(id+"F0.wireOp",EDGE,"E20")}),1.0]])]});
            extrude(context, id + "F1", {"entities" : qUnion([Q0, Q1, Q2, Q3, Q4, Q5, Q6, Q7, Q8, Q9, Q10, Q11, Q12, Q13, Q14, Q15, Q16, Q17, Q18, Q19, Q20, Q21, Q22, Q23, Q24]), "depth" : 25.4 * mm});
        }
    });
